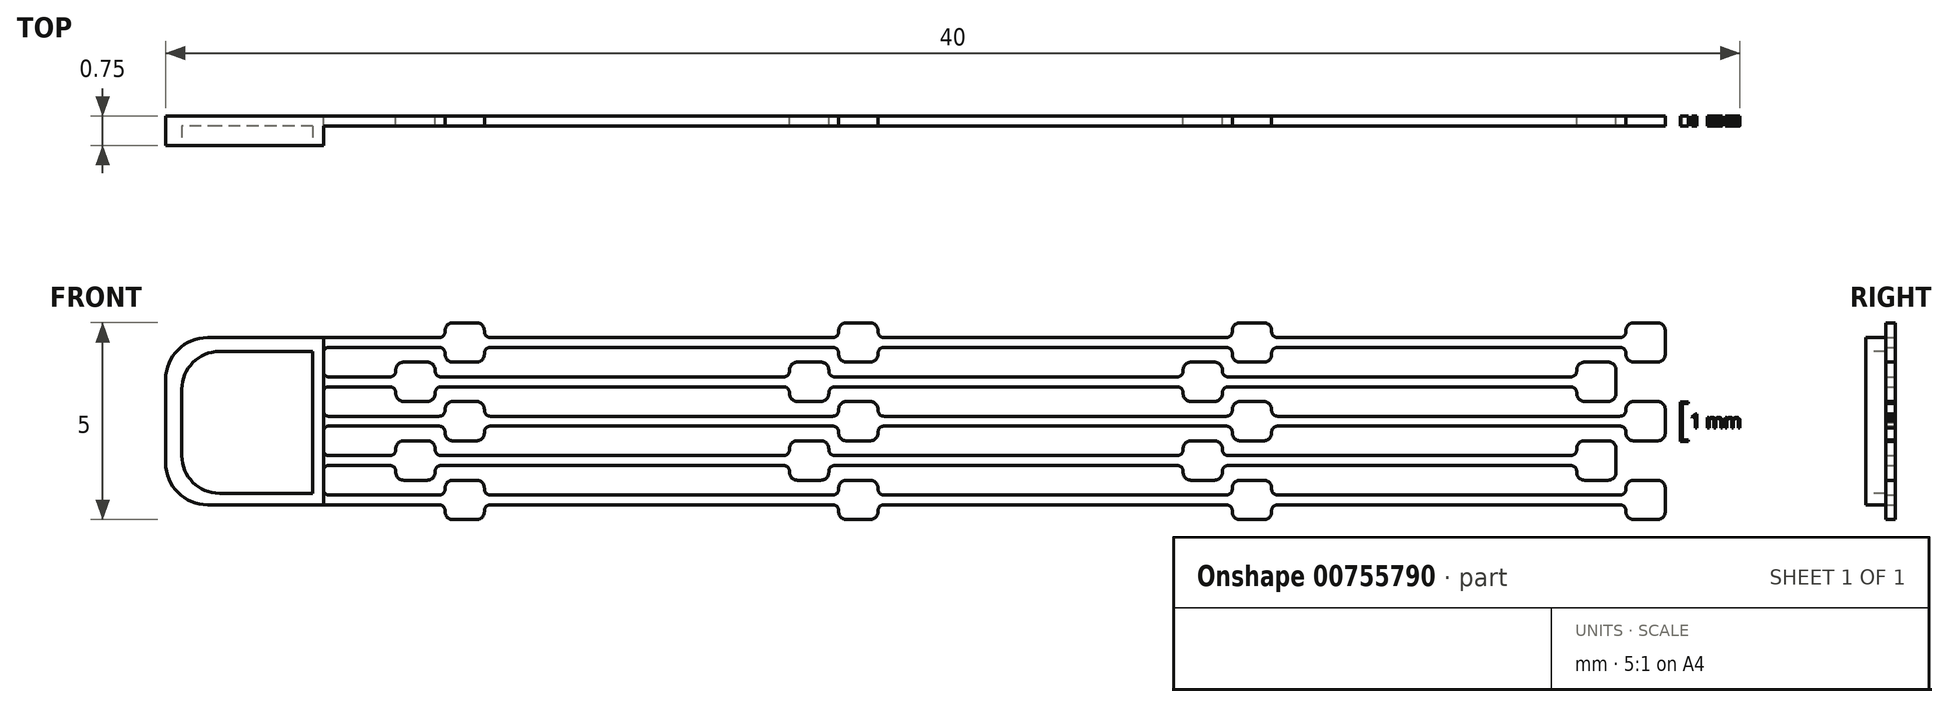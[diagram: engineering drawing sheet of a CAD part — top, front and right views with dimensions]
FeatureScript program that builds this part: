
annotation { "Feature Type Name" : "Feature", "Feature Type Description" : "" }
export const myFeature = defineFeature(function(context is Context, id is Id, definition is map)
    precondition{}
    {
        {
            var Q0;
            Q0=qCreatedBy(makeId("Front.planeOp"),FACE);
            var sketch = newSketch(context, id + "F0", { "sketchPlane" : qUnion([Q0])});
            skLineSegment(sketch, "E0.0.5.4", {"start": v(50.52, 28.02) * mm, "end": v(49.92, 28.02) * mm});
            skLineSegment(sketch, "E0.0.5.5", {"start": v(50.52, 27.02) * mm, "end": v(49.92, 27.02) * mm});
            skLineSegment(sketch, "E0.0.5.6", {"start": v(49.57, 27.4) * mm, "end": v(49.13, 27.4) * mm});
            skLineSegment(sketch, "E0.0.5.7", {"start": v(49.57, 27.64) * mm, "end": v(49.13, 27.64) * mm});
            skPoint(sketch, "E0.0.5.9", {"position": v(49.72, 27.64) * mm});
            skPoint(sketch, "E0.0.5.10", {"position": v(49.72, 28.02) * mm});
            skPoint(sketch, "E0.0.5.11", {"position": v(50.72, 27.4) * mm});
            skPoint(sketch, "E0.0.5.12", {"position": v(50.72, 28.02) * mm});
            skPoint(sketch, "E0.0.5.13", {"position": v(50.72, 27.64) * mm});
            skPoint(sketch, "E0.0.5.15", {"position": v(50.22, 27.52) * mm});
            skLineSegment(sketch, "E0.0.5.18", {"start": v(49.13, 27.4) * mm, "end": v(47.89, 27.4) * mm});
            skLineSegment(sketch, "E0.0.5.19", {"start": v(49.13, 27.64) * mm, "end": v(47.89, 27.64) * mm});
            skPoint(sketch, "E0.0.5.29", {"position": v(49.72, 27.4) * mm});
            skPoint(sketch, "E0.0.5.31", {"position": v(50.22, 27.52) * mm});
            skLineSegment(sketch, "E0.0.5.32", {"start": v(51.17, 27.4) * mm, "end": v(50.87, 27.4) * mm});
            skLineSegment(sketch, "E0.0.5.33", {"start": v(51.17, 27.64) * mm, "end": v(50.87, 27.64) * mm});
            skArc(sketch, "E0.0.5.34", {"start": v(50.72, 27.8) * mm, "mid": v(50.77, 27.69) * mm, "end": v(50.87, 27.64) * mm});
            skArc(sketch, "E0.0.5.41", {"start": v(50.52, 27.02) * mm, "mid": v(50.66, 27.08) * mm, "end": v(50.72, 27.22) * mm});
            skArc(sketch, "E0.0.5.44", {"start": v(49.72, 27.22) * mm, "mid": v(49.78, 27.08) * mm, "end": v(49.92, 27.02) * mm});
            skArc(sketch, "E0.0.5.45", {"start": v(49.92, 28.02) * mm, "mid": v(49.78, 27.96) * mm, "end": v(49.72, 27.82) * mm});
            skArc(sketch, "E0.0.5.46", {"start": v(50.72, 27.82) * mm, "mid": v(50.66, 27.96) * mm, "end": v(50.52, 28.02) * mm});
            skLineSegment(sketch, "E0.0.5.49", {"start": v(49.72, 27.22) * mm, "end": v(49.72, 27.24) * mm});
            skLineSegment(sketch, "E0.0.5.50", {"start": v(50.72, 27.22) * mm, "end": v(50.72, 27.24) * mm});
            skArc(sketch, "E0.0.5.55", {"start": v(49.72, 27.24) * mm, "mid": v(49.68, 27.35) * mm, "end": v(49.57, 27.4) * mm});
            skArc(sketch, "E0.0.5.56", {"start": v(50.87, 27.4) * mm, "mid": v(50.77, 27.35) * mm, "end": v(50.72, 27.24) * mm});
            skLineSegment(sketch, "E0.0.5.57", {"start": v(49.72, 27.8) * mm, "end": v(49.72, 27.82) * mm});
            skLineSegment(sketch, "E0.0.5.60", {"start": v(50.72, 27.8) * mm, "end": v(50.72, 27.82) * mm});
            skArc(sketch, "E0.0.5.61", {"start": v(49.57, 27.64) * mm, "mid": v(49.68, 27.69) * mm, "end": v(49.72, 27.8) * mm});
            skLineSegment(sketch, "E0.0.6.0", {"start": v(47.89, 28.4) * mm, "end": v(48.32, 28.4) * mm});
            skLineSegment(sketch, "E0.0.6.1", {"start": v(47.89, 28.64) * mm, "end": v(48.32, 28.64) * mm});
            skLineSegment(sketch, "E0.0.6.2", {"start": v(49.27, 29.02) * mm, "end": v(48.67, 29.02) * mm});
            skLineSegment(sketch, "E0.0.6.3", {"start": v(49.27, 28.02) * mm, "end": v(48.67, 28.02) * mm});
            skLineSegment(sketch, "E0.0.6.4", {"start": v(50.52, 30.02) * mm, "end": v(49.92, 30.02) * mm});
            skLineSegment(sketch, "E0.0.6.5", {"start": v(50.52, 29.02) * mm, "end": v(49.92, 29.02) * mm});
            skLineSegment(sketch, "E0.0.6.6", {"start": v(49.57, 29.4) * mm, "end": v(49.13, 29.4) * mm});
            skLineSegment(sketch, "E0.0.6.7", {"start": v(49.57, 29.64) * mm, "end": v(49.13, 29.64) * mm});
            skPoint(sketch, "E0.0.6.8", {"position": v(49.72, 29.02) * mm});
            skPoint(sketch, "E0.0.6.9", {"position": v(49.72, 29.64) * mm});
            skPoint(sketch, "E0.0.6.10", {"position": v(49.72, 30.02) * mm});
            skPoint(sketch, "E0.0.6.11", {"position": v(50.72, 29.4) * mm});
            skPoint(sketch, "E0.0.6.12", {"position": v(50.72, 30.02) * mm});
            skPoint(sketch, "E0.0.6.13", {"position": v(50.72, 29.64) * mm});
            skPoint(sketch, "E0.0.6.14", {"position": v(48.97, 28.52) * mm});
            skPoint(sketch, "E0.0.6.15", {"position": v(50.22, 29.52) * mm});
            skPoint(sketch, "E0.0.6.16", {"position": v(49.47, 28.02) * mm});
            skPoint(sketch, "E0.0.6.17", {"position": v(48.47, 28.4) * mm});
            skLineSegment(sketch, "E0.0.6.18", {"start": v(49.13, 29.4) * mm, "end": v(47.89, 29.4) * mm});
            skLineSegment(sketch, "E0.0.6.19", {"start": v(49.13, 29.64) * mm, "end": v(47.89, 29.64) * mm});
            skPoint(sketch, "E0.0.6.20", {"position": v(48.47, 28.02) * mm});
            skPoint(sketch, "E0.0.6.21", {"position": v(48.47, 28.64) * mm});
            skLineSegment(sketch, "E0.0.6.22", {"start": v(49.62, 28.4) * mm, "end": v(51.17, 28.4) * mm});
            skPoint(sketch, "E0.0.6.23", {"position": v(48.47, 29.02) * mm});
            skPoint(sketch, "E0.0.6.24", {"position": v(49.47, 28.4) * mm});
            skLineSegment(sketch, "E0.0.6.25", {"start": v(49.62, 28.64) * mm, "end": v(51.17, 28.64) * mm});
            skPoint(sketch, "E0.0.6.26", {"position": v(49.47, 29.02) * mm});
            skPoint(sketch, "E0.0.6.27", {"position": v(49.47, 28.64) * mm});
            skPoint(sketch, "E0.0.6.28", {"position": v(50.72, 29.02) * mm});
            skPoint(sketch, "E0.0.6.29", {"position": v(49.72, 29.4) * mm});
            skPoint(sketch, "E0.0.6.30", {"position": v(48.97, 28.52) * mm});
            skPoint(sketch, "E0.0.6.31", {"position": v(50.22, 29.52) * mm});
            skLineSegment(sketch, "E0.0.6.32", {"start": v(51.17, 29.4) * mm, "end": v(50.87, 29.4) * mm});
            skLineSegment(sketch, "E0.0.6.33", {"start": v(51.17, 29.64) * mm, "end": v(50.87, 29.64) * mm});
            skArc(sketch, "E0.0.6.34", {"start": v(50.72, 29.8) * mm, "mid": v(50.77, 29.69) * mm, "end": v(50.87, 29.64) * mm});
            skArc(sketch, "E0.0.6.35", {"start": v(49.27, 28.02) * mm, "mid": v(49.41, 28.08) * mm, "end": v(49.47, 28.22) * mm});
            skArc(sketch, "E0.0.6.36", {"start": v(48.47, 28.22) * mm, "mid": v(48.53, 28.08) * mm, "end": v(48.67, 28.02) * mm});
            skArc(sketch, "E0.0.6.37", {"start": v(48.67, 29.02) * mm, "mid": v(48.53, 28.96) * mm, "end": v(48.47, 28.82) * mm});
            skArc(sketch, "E0.0.6.39", {"start": v(49.47, 28.82) * mm, "mid": v(49.41, 28.96) * mm, "end": v(49.27, 29.02) * mm});
            skArc(sketch, "E0.0.6.41", {"start": v(50.52, 29.02) * mm, "mid": v(50.66, 29.08) * mm, "end": v(50.72, 29.22) * mm});
            skArc(sketch, "E0.0.6.44", {"start": v(49.72, 29.22) * mm, "mid": v(49.78, 29.08) * mm, "end": v(49.92, 29.02) * mm});
            skArc(sketch, "E0.0.6.45", {"start": v(49.92, 30.02) * mm, "mid": v(49.78, 29.96) * mm, "end": v(49.72, 29.82) * mm});
            skArc(sketch, "E0.0.6.46", {"start": v(50.72, 29.82) * mm, "mid": v(50.66, 29.96) * mm, "end": v(50.52, 30.02) * mm});
            skArc(sketch, "E0.0.6.47", {"start": v(48.47, 28.24) * mm, "mid": v(48.43, 28.35) * mm, "end": v(48.32, 28.4) * mm});
            skArc(sketch, "E0.0.6.48", {"start": v(49.62, 28.4) * mm, "mid": v(49.52, 28.35) * mm, "end": v(49.47, 28.24) * mm});
            skLineSegment(sketch, "E0.0.6.49", {"start": v(49.72, 29.22) * mm, "end": v(49.72, 29.24) * mm});
            skLineSegment(sketch, "E0.0.6.50", {"start": v(50.72, 29.22) * mm, "end": v(50.72, 29.24) * mm});
            skArc(sketch, "E0.0.6.51", {"start": v(48.32, 28.64) * mm, "mid": v(48.43, 28.69) * mm, "end": v(48.47, 28.8) * mm});
            skLineSegment(sketch, "E0.0.6.52", {"start": v(48.47, 28.8) * mm, "end": v(48.47, 28.82) * mm});
            skArc(sketch, "E0.0.6.53", {"start": v(49.47, 28.8) * mm, "mid": v(49.52, 28.69) * mm, "end": v(49.62, 28.64) * mm});
            skLineSegment(sketch, "E0.0.6.54", {"start": v(49.47, 28.8) * mm, "end": v(49.47, 28.82) * mm});
            skArc(sketch, "E0.0.6.55", {"start": v(49.72, 29.24) * mm, "mid": v(49.68, 29.35) * mm, "end": v(49.57, 29.4) * mm});
            skArc(sketch, "E0.0.6.56", {"start": v(50.87, 29.4) * mm, "mid": v(50.77, 29.35) * mm, "end": v(50.72, 29.24) * mm});
            skLineSegment(sketch, "E0.0.6.57", {"start": v(49.72, 29.8) * mm, "end": v(49.72, 29.82) * mm});
            skLineSegment(sketch, "E0.0.6.58", {"start": v(48.47, 28.22) * mm, "end": v(48.47, 28.24) * mm});
            skLineSegment(sketch, "E0.0.6.59", {"start": v(49.47, 28.22) * mm, "end": v(49.47, 28.24) * mm});
            skLineSegment(sketch, "E0.0.6.60", {"start": v(50.72, 29.8) * mm, "end": v(50.72, 29.82) * mm});
            skArc(sketch, "E0.0.6.61", {"start": v(49.57, 29.64) * mm, "mid": v(49.68, 29.69) * mm, "end": v(49.72, 29.8) * mm});
            skLineSegment(sketch, "E0.0.7.0", {"start": v(47.89, 30.4) * mm, "end": v(48.32, 30.4) * mm});
            skLineSegment(sketch, "E0.0.7.1", {"start": v(47.89, 30.64) * mm, "end": v(48.32, 30.64) * mm});
            skLineSegment(sketch, "E0.0.7.2", {"start": v(49.27, 31.02) * mm, "end": v(48.67, 31.02) * mm});
            skLineSegment(sketch, "E0.0.7.3", {"start": v(49.27, 30.02) * mm, "end": v(48.67, 30.02) * mm});
            skLineSegment(sketch, "E0.0.7.4", {"start": v(50.52, 32.02) * mm, "end": v(49.92, 32.02) * mm});
            skLineSegment(sketch, "E0.0.7.5", {"start": v(50.52, 31.02) * mm, "end": v(49.92, 31.02) * mm});
            skLineSegment(sketch, "E0.0.7.6", {"start": v(49.57, 31.4) * mm, "end": v(49.13, 31.4) * mm});
            skLineSegment(sketch, "E0.0.7.7", {"start": v(49.57, 31.64) * mm, "end": v(49.13, 31.64) * mm});
            skPoint(sketch, "E0.0.7.8", {"position": v(49.72, 31.02) * mm});
            skPoint(sketch, "E0.0.7.9", {"position": v(49.72, 31.64) * mm});
            skPoint(sketch, "E0.0.7.10", {"position": v(49.72, 32.02) * mm});
            skPoint(sketch, "E0.0.7.11", {"position": v(50.72, 31.4) * mm});
            skPoint(sketch, "E0.0.7.12", {"position": v(50.72, 32.02) * mm});
            skPoint(sketch, "E0.0.7.13", {"position": v(50.72, 31.64) * mm});
            skPoint(sketch, "E0.0.7.14", {"position": v(48.97, 30.52) * mm});
            skPoint(sketch, "E0.0.7.15", {"position": v(50.22, 31.52) * mm});
            skPoint(sketch, "E0.0.7.16", {"position": v(49.47, 30.02) * mm});
            skPoint(sketch, "E0.0.7.17", {"position": v(48.47, 30.4) * mm});
            skLineSegment(sketch, "E0.0.7.18", {"start": v(49.13, 31.4) * mm, "end": v(47.89, 31.4) * mm});
            skLineSegment(sketch, "E0.0.7.19", {"start": v(49.13, 31.64) * mm, "end": v(47.89, 31.64) * mm});
            skPoint(sketch, "E0.0.7.20", {"position": v(48.47, 30.02) * mm});
            skPoint(sketch, "E0.0.7.21", {"position": v(48.47, 30.64) * mm});
            skLineSegment(sketch, "E0.0.7.22", {"start": v(49.62, 30.4) * mm, "end": v(51.17, 30.4) * mm});
            skPoint(sketch, "E0.0.7.23", {"position": v(48.47, 31.02) * mm});
            skPoint(sketch, "E0.0.7.24", {"position": v(49.47, 30.4) * mm});
            skLineSegment(sketch, "E0.0.7.25", {"start": v(49.62, 30.64) * mm, "end": v(51.17, 30.64) * mm});
            skPoint(sketch, "E0.0.7.26", {"position": v(49.47, 31.02) * mm});
            skPoint(sketch, "E0.0.7.27", {"position": v(49.47, 30.64) * mm});
            skPoint(sketch, "E0.0.7.28", {"position": v(50.72, 31.02) * mm});
            skPoint(sketch, "E0.0.7.29", {"position": v(49.72, 31.4) * mm});
            skPoint(sketch, "E0.0.7.30", {"position": v(48.97, 30.52) * mm});
            skPoint(sketch, "E0.0.7.31", {"position": v(50.22, 31.52) * mm});
            skLineSegment(sketch, "E0.0.7.32", {"start": v(51.17, 31.4) * mm, "end": v(50.87, 31.4) * mm});
            skLineSegment(sketch, "E0.0.7.33", {"start": v(51.17, 31.64) * mm, "end": v(50.87, 31.64) * mm});
            skArc(sketch, "E0.0.7.34", {"start": v(50.72, 31.8) * mm, "mid": v(50.77, 31.69) * mm, "end": v(50.87, 31.64) * mm});
            skArc(sketch, "E0.0.7.35", {"start": v(49.27, 30.02) * mm, "mid": v(49.41, 30.08) * mm, "end": v(49.47, 30.22) * mm});
            skArc(sketch, "E0.0.7.36", {"start": v(48.47, 30.22) * mm, "mid": v(48.53, 30.08) * mm, "end": v(48.67, 30.02) * mm});
            skArc(sketch, "E0.0.7.37", {"start": v(48.67, 31.02) * mm, "mid": v(48.53, 30.96) * mm, "end": v(48.47, 30.82) * mm});
            skArc(sketch, "E0.0.7.39", {"start": v(49.47, 30.82) * mm, "mid": v(49.41, 30.96) * mm, "end": v(49.27, 31.02) * mm});
            skArc(sketch, "E0.0.7.41", {"start": v(50.52, 31.02) * mm, "mid": v(50.66, 31.08) * mm, "end": v(50.72, 31.22) * mm});
            skArc(sketch, "E0.0.7.44", {"start": v(49.72, 31.22) * mm, "mid": v(49.78, 31.08) * mm, "end": v(49.92, 31.02) * mm});
            skArc(sketch, "E0.0.7.45", {"start": v(49.92, 32.02) * mm, "mid": v(49.78, 31.96) * mm, "end": v(49.72, 31.82) * mm});
            skArc(sketch, "E0.0.7.46", {"start": v(50.72, 31.82) * mm, "mid": v(50.66, 31.96) * mm, "end": v(50.52, 32.02) * mm});
            skArc(sketch, "E0.0.7.47", {"start": v(48.47, 30.24) * mm, "mid": v(48.43, 30.35) * mm, "end": v(48.32, 30.4) * mm});
            skArc(sketch, "E0.0.7.48", {"start": v(49.62, 30.4) * mm, "mid": v(49.52, 30.35) * mm, "end": v(49.47, 30.24) * mm});
            skLineSegment(sketch, "E0.0.7.49", {"start": v(49.72, 31.22) * mm, "end": v(49.72, 31.24) * mm});
            skLineSegment(sketch, "E0.0.7.50", {"start": v(50.72, 31.22) * mm, "end": v(50.72, 31.24) * mm});
            skArc(sketch, "E0.0.7.51", {"start": v(48.32, 30.64) * mm, "mid": v(48.43, 30.69) * mm, "end": v(48.47, 30.8) * mm});
            skLineSegment(sketch, "E0.0.7.52", {"start": v(48.47, 30.8) * mm, "end": v(48.47, 30.82) * mm});
            skArc(sketch, "E0.0.7.53", {"start": v(49.47, 30.8) * mm, "mid": v(49.52, 30.69) * mm, "end": v(49.62, 30.64) * mm});
            skLineSegment(sketch, "E0.0.7.54", {"start": v(49.47, 30.8) * mm, "end": v(49.47, 30.82) * mm});
            skArc(sketch, "E0.0.7.55", {"start": v(49.72, 31.24) * mm, "mid": v(49.68, 31.35) * mm, "end": v(49.57, 31.4) * mm});
            skArc(sketch, "E0.0.7.56", {"start": v(50.87, 31.4) * mm, "mid": v(50.77, 31.35) * mm, "end": v(50.72, 31.24) * mm});
            skLineSegment(sketch, "E0.0.7.57", {"start": v(49.72, 31.8) * mm, "end": v(49.72, 31.82) * mm});
            skLineSegment(sketch, "E0.0.7.58", {"start": v(48.47, 30.22) * mm, "end": v(48.47, 30.24) * mm});
            skLineSegment(sketch, "E0.0.7.59", {"start": v(49.47, 30.22) * mm, "end": v(49.47, 30.24) * mm});
            skLineSegment(sketch, "E0.0.7.60", {"start": v(50.72, 31.8) * mm, "end": v(50.72, 31.82) * mm});
            skArc(sketch, "E0.0.7.61", {"start": v(49.57, 31.64) * mm, "mid": v(49.68, 31.69) * mm, "end": v(49.72, 31.8) * mm});
            skPoint(sketch, "E1.1.0.2", {"position": v(59.72, 32.02) * mm});
            skPoint(sketch, "E1.1.0.3", {"position": v(60.72, 32.02) * mm});
            skPoint(sketch, "E1.1.0.6", {"position": v(60.72, 31.64) * mm});
            skPoint(sketch, "E1.1.0.8", {"position": v(58.47, 28.02) * mm});
            skPoint(sketch, "E1.1.0.11", {"position": v(60.22, 31.52) * mm});
            skPoint(sketch, "E1.1.0.14", {"position": v(59.47, 30.02) * mm});
            skPoint(sketch, "E1.1.0.15", {"position": v(58.47, 29.02) * mm});
            skPoint(sketch, "E1.1.0.17", {"position": v(59.72, 28.02) * mm});
            skPoint(sketch, "E1.1.0.20", {"position": v(58.47, 30.02) * mm});
            skPoint(sketch, "E1.1.0.21", {"position": v(60.72, 27.4) * mm});
            skPoint(sketch, "E1.1.0.22", {"position": v(58.47, 30.64) * mm});
            skPoint(sketch, "E1.1.0.32", {"position": v(60.72, 29.02) * mm});
            skPoint(sketch, "E1.1.0.33", {"position": v(58.47, 31.02) * mm});
            skPoint(sketch, "E1.1.0.34", {"position": v(60.72, 28.02) * mm});
            skPoint(sketch, "E1.1.0.35", {"position": v(59.72, 29.02) * mm});
            skPoint(sketch, "E1.1.0.38", {"position": v(59.72, 31.64) * mm});
            skPoint(sketch, "E1.1.0.39", {"position": v(60.72, 29.64) * mm});
            skPoint(sketch, "E1.1.0.43", {"position": v(60.22, 31.52) * mm});
            skPoint(sketch, "E1.1.0.44", {"position": v(60.72, 31.4) * mm});
            skPoint(sketch, "E1.1.0.49", {"position": v(58.47, 28.4) * mm});
            skPoint(sketch, "E1.1.0.52", {"position": v(58.97, 30.52) * mm});
            skPoint(sketch, "E1.1.0.57", {"position": v(58.47, 28.64) * mm});
            skPoint(sketch, "E1.1.0.67", {"position": v(59.72, 27.64) * mm});
            skPoint(sketch, "E1.1.0.68", {"position": v(58.47, 30.4) * mm});
            skPoint(sketch, "E1.1.0.69", {"position": v(59.47, 28.4) * mm});
            skPoint(sketch, "E1.1.0.71", {"position": v(60.22, 27.52) * mm});
            skPoint(sketch, "E1.1.0.72", {"position": v(59.47, 28.64) * mm});
            skPoint(sketch, "E1.1.0.78", {"position": v(59.72, 31.4) * mm});
            skPoint(sketch, "E1.1.0.80", {"position": v(60.72, 30.02) * mm});
            skPoint(sketch, "E1.1.0.82", {"position": v(60.22, 27.52) * mm});
            skPoint(sketch, "E1.1.0.83", {"position": v(60.72, 29.4) * mm});
            skPoint(sketch, "E1.1.0.85", {"position": v(60.72, 31.02) * mm});
            skPoint(sketch, "E1.1.0.88", {"position": v(58.97, 28.52) * mm});
            skPoint(sketch, "E1.1.0.90", {"position": v(58.97, 30.52) * mm});
            skPoint(sketch, "E1.1.0.92", {"position": v(60.22, 29.52) * mm});
            skPoint(sketch, "E1.1.0.94", {"position": v(60.72, 27.64) * mm});
            skPoint(sketch, "E1.1.0.106", {"position": v(59.72, 27.4) * mm});
            skPoint(sketch, "E1.1.0.110", {"position": v(59.47, 29.02) * mm});
            skPoint(sketch, "E1.1.0.113", {"position": v(60.22, 29.52) * mm});
            skPoint(sketch, "E1.1.0.117", {"position": v(59.72, 31.02) * mm});
            skPoint(sketch, "E1.1.0.126", {"position": v(59.47, 28.02) * mm});
            skPoint(sketch, "E1.1.0.134", {"position": v(58.97, 28.52) * mm});
            skPoint(sketch, "E1.1.0.141", {"position": v(59.47, 30.64) * mm});
            skPoint(sketch, "E1.1.0.147", {"position": v(59.72, 30.02) * mm});
            skPoint(sketch, "E1.1.0.148", {"position": v(59.47, 31.02) * mm});
            skPoint(sketch, "E1.1.0.154", {"position": v(59.47, 30.4) * mm});
            skPoint(sketch, "E1.1.0.155", {"position": v(59.72, 29.4) * mm});
            skPoint(sketch, "E1.1.0.156", {"position": v(59.72, 29.64) * mm});
            skLineSegment(sketch, "E1.1.0.161", {"start": v(59.13, 31.64) * mm, "end": v(57.89, 31.64) * mm});
            skLineSegment(sketch, "E1.1.0.162", {"start": v(59.13, 31.4) * mm, "end": v(57.89, 31.4) * mm});
            skLineSegment(sketch, "E1.1.0.163", {"start": v(57.89, 30.64) * mm, "end": v(58.32, 30.64) * mm});
            skLineSegment(sketch, "E1.1.0.166", {"start": v(57.89, 30.4) * mm, "end": v(58.32, 30.4) * mm});
            skLineSegment(sketch, "E1.1.0.171", {"start": v(59.13, 29.64) * mm, "end": v(57.89, 29.64) * mm});
            skLineSegment(sketch, "E1.1.0.173", {"start": v(59.13, 29.4) * mm, "end": v(57.89, 29.4) * mm});
            skLineSegment(sketch, "E1.1.0.174", {"start": v(59.13, 27.64) * mm, "end": v(57.89, 27.64) * mm});
            skArc(sketch, "E1.1.0.175", {"start": v(58.47, 28.22) * mm, "mid": v(58.53, 28.08) * mm, "end": v(58.67, 28.02) * mm});
            skLineSegment(sketch, "E1.1.0.176", {"start": v(57.89, 28.4) * mm, "end": v(58.32, 28.4) * mm});
            skLineSegment(sketch, "E1.1.0.177", {"start": v(57.89, 28.64) * mm, "end": v(58.32, 28.64) * mm});
            skLineSegment(sketch, "E1.1.0.180", {"start": v(60.52, 32.02) * mm, "end": v(59.92, 32.02) * mm});
            skLineSegment(sketch, "E1.1.0.185", {"start": v(61.17, 31.64) * mm, "end": v(60.87, 31.64) * mm});
            skLineSegment(sketch, "E1.1.0.194", {"start": v(59.13, 27.4) * mm, "end": v(57.89, 27.4) * mm});
            skLineSegment(sketch, "E1.1.0.205", {"start": v(61.17, 31.4) * mm, "end": v(60.87, 31.4) * mm});
            skArc(sketch, "E1.1.0.215", {"start": v(59.57, 31.64) * mm, "mid": v(59.68, 31.69) * mm, "end": v(59.72, 31.8) * mm});
            skArc(sketch, "E1.1.0.216", {"start": v(60.72, 31.82) * mm, "mid": v(60.66, 31.96) * mm, "end": v(60.52, 32.02) * mm});
            skArc(sketch, "E1.1.0.218", {"start": v(60.72, 31.8) * mm, "mid": v(60.77, 31.69) * mm, "end": v(60.87, 31.64) * mm});
            skLineSegment(sketch, "E1.1.0.222", {"start": v(61.17, 29.64) * mm, "end": v(60.87, 29.64) * mm});
            skLineSegment(sketch, "E1.1.0.228", {"start": v(59.72, 31.8) * mm, "end": v(59.72, 31.82) * mm});
            skLineSegment(sketch, "E1.1.0.229", {"start": v(60.72, 31.8) * mm, "end": v(60.72, 31.82) * mm});
            skLineSegment(sketch, "E1.1.0.230", {"start": v(59.62, 30.64) * mm, "end": v(61.17, 30.64) * mm});
            skArc(sketch, "E1.1.0.231", {"start": v(59.92, 32.02) * mm, "mid": v(59.78, 31.96) * mm, "end": v(59.72, 31.82) * mm});
            skLineSegment(sketch, "E1.1.0.239", {"start": v(59.27, 31.02) * mm, "end": v(58.67, 31.02) * mm});
            skLineSegment(sketch, "E1.1.0.240", {"start": v(61.17, 29.4) * mm, "end": v(60.87, 29.4) * mm});
            skLineSegment(sketch, "E1.1.0.242", {"start": v(59.57, 31.64) * mm, "end": v(59.13, 31.64) * mm});
            skArc(sketch, "E1.1.0.243", {"start": v(59.47, 30.82) * mm, "mid": v(59.41, 30.96) * mm, "end": v(59.27, 31.02) * mm});
            skArc(sketch, "E1.1.0.244", {"start": v(59.72, 31.24) * mm, "mid": v(59.68, 31.35) * mm, "end": v(59.57, 31.4) * mm});
            skArc(sketch, "E1.1.0.246", {"start": v(60.87, 31.4) * mm, "mid": v(60.77, 31.35) * mm, "end": v(60.72, 31.24) * mm});
            skLineSegment(sketch, "E1.1.0.249", {"start": v(59.57, 31.4) * mm, "end": v(59.13, 31.4) * mm});
            skLineSegment(sketch, "E1.1.0.250", {"start": v(60.52, 31.02) * mm, "end": v(59.92, 31.02) * mm});
            skArc(sketch, "E1.1.0.251", {"start": v(60.52, 31.02) * mm, "mid": v(60.66, 31.08) * mm, "end": v(60.72, 31.22) * mm});
            skLineSegment(sketch, "E1.1.0.253", {"start": v(59.62, 30.4) * mm, "end": v(61.17, 30.4) * mm});
            skLineSegment(sketch, "E1.1.0.257", {"start": v(59.72, 31.22) * mm, "end": v(59.72, 31.24) * mm});
            skLineSegment(sketch, "E1.1.0.259", {"start": v(60.72, 31.22) * mm, "end": v(60.72, 31.24) * mm});
            skArc(sketch, "E1.1.0.260", {"start": v(58.32, 30.64) * mm, "mid": v(58.43, 30.69) * mm, "end": v(58.47, 30.8) * mm});
            skArc(sketch, "E1.1.0.264", {"start": v(58.67, 31.02) * mm, "mid": v(58.53, 30.96) * mm, "end": v(58.47, 30.82) * mm});
            skLineSegment(sketch, "E1.1.0.265", {"start": v(59.62, 28.64) * mm, "end": v(61.17, 28.64) * mm});
            skArc(sketch, "E1.1.0.266", {"start": v(59.47, 30.8) * mm, "mid": v(59.52, 30.69) * mm, "end": v(59.62, 30.64) * mm});
            skLineSegment(sketch, "E1.1.0.269", {"start": v(59.47, 30.8) * mm, "end": v(59.47, 30.82) * mm});
            skLineSegment(sketch, "E1.1.0.274", {"start": v(61.17, 27.4) * mm, "end": v(60.87, 27.4) * mm});
            skArc(sketch, "E1.1.0.275", {"start": v(58.47, 30.24) * mm, "mid": v(58.43, 30.35) * mm, "end": v(58.32, 30.4) * mm});
            skLineSegment(sketch, "E1.1.0.276", {"start": v(61.17, 27.64) * mm, "end": v(60.87, 27.64) * mm});
            skArc(sketch, "E1.1.0.278", {"start": v(59.72, 31.22) * mm, "mid": v(59.78, 31.08) * mm, "end": v(59.92, 31.02) * mm});
            skArc(sketch, "E1.1.0.280", {"start": v(59.62, 30.4) * mm, "mid": v(59.52, 30.35) * mm, "end": v(59.47, 30.24) * mm});
            skLineSegment(sketch, "E1.1.0.284", {"start": v(59.62, 28.4) * mm, "end": v(61.17, 28.4) * mm});
            skLineSegment(sketch, "E1.1.0.285", {"start": v(58.47, 30.8) * mm, "end": v(58.47, 30.82) * mm});
            skLineSegment(sketch, "E1.1.0.288", {"start": v(60.52, 29.02) * mm, "end": v(59.92, 29.02) * mm});
            skArc(sketch, "E1.1.0.289", {"start": v(59.47, 28.82) * mm, "mid": v(59.41, 28.96) * mm, "end": v(59.27, 29.02) * mm});
            skLineSegment(sketch, "E1.1.0.290", {"start": v(60.52, 30.02) * mm, "end": v(59.92, 30.02) * mm});
            skLineSegment(sketch, "E1.1.0.292", {"start": v(59.27, 29.02) * mm, "end": v(58.67, 29.02) * mm});
            skLineSegment(sketch, "E1.1.0.293", {"start": v(59.27, 28.02) * mm, "end": v(58.67, 28.02) * mm});
            skLineSegment(sketch, "E1.1.0.295", {"start": v(59.57, 29.64) * mm, "end": v(59.13, 29.64) * mm});
            skArc(sketch, "E1.1.0.298", {"start": v(59.92, 30.02) * mm, "mid": v(59.78, 29.96) * mm, "end": v(59.72, 29.82) * mm});
            skArc(sketch, "E1.1.0.299", {"start": v(59.57, 29.64) * mm, "mid": v(59.68, 29.69) * mm, "end": v(59.72, 29.8) * mm});
            skArc(sketch, "E1.1.0.301", {"start": v(60.72, 29.82) * mm, "mid": v(60.66, 29.96) * mm, "end": v(60.52, 30.02) * mm});
            skArc(sketch, "E1.1.0.304", {"start": v(58.47, 28.24) * mm, "mid": v(58.43, 28.35) * mm, "end": v(58.32, 28.4) * mm});
            skArc(sketch, "E1.1.0.305", {"start": v(58.67, 29.02) * mm, "mid": v(58.53, 28.96) * mm, "end": v(58.47, 28.82) * mm});
            skArc(sketch, "E1.1.0.308", {"start": v(59.62, 28.4) * mm, "mid": v(59.52, 28.35) * mm, "end": v(59.47, 28.24) * mm});
            skLineSegment(sketch, "E1.1.0.311", {"start": v(59.27, 30.02) * mm, "end": v(58.67, 30.02) * mm});
            skLineSegment(sketch, "E1.1.0.312", {"start": v(59.72, 29.22) * mm, "end": v(59.72, 29.24) * mm});
            skLineSegment(sketch, "E1.1.0.315", {"start": v(60.72, 29.22) * mm, "end": v(60.72, 29.24) * mm});
            skArc(sketch, "E1.1.0.316", {"start": v(60.72, 29.8) * mm, "mid": v(60.77, 29.69) * mm, "end": v(60.87, 29.64) * mm});
            skArc(sketch, "E1.1.0.317", {"start": v(59.92, 28.02) * mm, "mid": v(59.78, 27.96) * mm, "end": v(59.72, 27.82) * mm});
            skLineSegment(sketch, "E1.1.0.326", {"start": v(58.47, 30.22) * mm, "end": v(58.47, 30.24) * mm});
            skLineSegment(sketch, "E1.1.0.327", {"start": v(58.47, 28.8) * mm, "end": v(58.47, 28.82) * mm});
            skArc(sketch, "E1.1.0.328", {"start": v(60.72, 27.82) * mm, "mid": v(60.66, 27.96) * mm, "end": v(60.52, 28.02) * mm});
            skArc(sketch, "E1.1.0.333", {"start": v(59.27, 28.02) * mm, "mid": v(59.41, 28.08) * mm, "end": v(59.47, 28.22) * mm});
            skArc(sketch, "E1.1.0.337", {"start": v(60.52, 29.02) * mm, "mid": v(60.66, 29.08) * mm, "end": v(60.72, 29.22) * mm});
            skLineSegment(sketch, "E1.1.0.340", {"start": v(59.72, 29.8) * mm, "end": v(59.72, 29.82) * mm});
            skLineSegment(sketch, "E1.1.0.343", {"start": v(59.57, 29.4) * mm, "end": v(59.13, 29.4) * mm});
            skLineSegment(sketch, "E1.1.0.345", {"start": v(58.47, 28.22) * mm, "end": v(58.47, 28.24) * mm});
            skLineSegment(sketch, "E1.1.0.349", {"start": v(59.47, 28.22) * mm, "end": v(59.47, 28.24) * mm});
            skArc(sketch, "E1.1.0.356", {"start": v(59.72, 29.22) * mm, "mid": v(59.78, 29.08) * mm, "end": v(59.92, 29.02) * mm});
            skLineSegment(sketch, "E1.1.0.357", {"start": v(60.72, 29.8) * mm, "end": v(60.72, 29.82) * mm});
            skArc(sketch, "E1.1.0.363", {"start": v(59.27, 30.02) * mm, "mid": v(59.41, 30.08) * mm, "end": v(59.47, 30.22) * mm});
            skLineSegment(sketch, "E1.1.0.369", {"start": v(60.52, 28.02) * mm, "end": v(59.92, 28.02) * mm});
            skArc(sketch, "E1.1.0.371", {"start": v(58.47, 30.22) * mm, "mid": v(58.53, 30.08) * mm, "end": v(58.67, 30.02) * mm});
            skArc(sketch, "E1.1.0.374", {"start": v(60.52, 27.02) * mm, "mid": v(60.66, 27.08) * mm, "end": v(60.72, 27.22) * mm});
            skLineSegment(sketch, "E1.1.0.375", {"start": v(60.52, 27.02) * mm, "end": v(59.92, 27.02) * mm});
            skLineSegment(sketch, "E1.1.0.377", {"start": v(59.57, 27.4) * mm, "end": v(59.13, 27.4) * mm});
            skLineSegment(sketch, "E1.1.0.382", {"start": v(59.57, 27.64) * mm, "end": v(59.13, 27.64) * mm});
            skArc(sketch, "E1.1.0.383", {"start": v(59.47, 28.8) * mm, "mid": v(59.52, 28.69) * mm, "end": v(59.62, 28.64) * mm});
            skLineSegment(sketch, "E1.1.0.385", {"start": v(60.72, 27.8) * mm, "end": v(60.72, 27.82) * mm});
            skArc(sketch, "E1.1.0.386", {"start": v(59.72, 27.22) * mm, "mid": v(59.78, 27.08) * mm, "end": v(59.92, 27.02) * mm});
            skArc(sketch, "E1.1.0.390", {"start": v(59.57, 27.64) * mm, "mid": v(59.68, 27.69) * mm, "end": v(59.72, 27.8) * mm});
            skArc(sketch, "E1.1.0.397", {"start": v(58.32, 28.64) * mm, "mid": v(58.43, 28.69) * mm, "end": v(58.47, 28.8) * mm});
            skArc(sketch, "E1.1.0.399", {"start": v(60.72, 27.8) * mm, "mid": v(60.77, 27.69) * mm, "end": v(60.87, 27.64) * mm});
            skLineSegment(sketch, "E1.1.0.402", {"start": v(59.47, 28.8) * mm, "end": v(59.47, 28.82) * mm});
            skArc(sketch, "E1.1.0.403", {"start": v(60.87, 29.4) * mm, "mid": v(60.77, 29.35) * mm, "end": v(60.72, 29.24) * mm});
            skArc(sketch, "E1.1.0.410", {"start": v(59.72, 29.24) * mm, "mid": v(59.68, 29.35) * mm, "end": v(59.57, 29.4) * mm});
            skArc(sketch, "E1.1.0.418", {"start": v(59.72, 27.24) * mm, "mid": v(59.68, 27.35) * mm, "end": v(59.57, 27.4) * mm});
            skArc(sketch, "E1.1.0.421", {"start": v(60.87, 27.4) * mm, "mid": v(60.77, 27.35) * mm, "end": v(60.72, 27.24) * mm});
            skLineSegment(sketch, "E1.1.0.423", {"start": v(59.72, 27.8) * mm, "end": v(59.72, 27.82) * mm});
            skLineSegment(sketch, "E1.1.0.426", {"start": v(59.47, 30.22) * mm, "end": v(59.47, 30.24) * mm});
            skLineSegment(sketch, "E1.1.0.430", {"start": v(59.72, 27.22) * mm, "end": v(59.72, 27.24) * mm});
            skLineSegment(sketch, "E1.1.0.432", {"start": v(60.72, 27.22) * mm, "end": v(60.72, 27.24) * mm});
            skPoint(sketch, "E1.2.0.2", {"position": v(69.72, 32.02) * mm});
            skPoint(sketch, "E1.2.0.3", {"position": v(70.72, 32.02) * mm});
            skPoint(sketch, "E1.2.0.6", {"position": v(70.72, 31.64) * mm});
            skPoint(sketch, "E1.2.0.8", {"position": v(68.47, 28.02) * mm});
            skPoint(sketch, "E1.2.0.11", {"position": v(70.22, 31.52) * mm});
            skPoint(sketch, "E1.2.0.14", {"position": v(69.47, 30.02) * mm});
            skPoint(sketch, "E1.2.0.15", {"position": v(68.47, 29.02) * mm});
            skPoint(sketch, "E1.2.0.17", {"position": v(69.72, 28.02) * mm});
            skPoint(sketch, "E1.2.0.20", {"position": v(68.47, 30.02) * mm});
            skPoint(sketch, "E1.2.0.21", {"position": v(70.72, 27.4) * mm});
            skPoint(sketch, "E1.2.0.22", {"position": v(68.47, 30.64) * mm});
            skPoint(sketch, "E1.2.0.32", {"position": v(70.72, 29.02) * mm});
            skPoint(sketch, "E1.2.0.33", {"position": v(68.47, 31.02) * mm});
            skPoint(sketch, "E1.2.0.34", {"position": v(70.72, 28.02) * mm});
            skPoint(sketch, "E1.2.0.35", {"position": v(69.72, 29.02) * mm});
            skPoint(sketch, "E1.2.0.38", {"position": v(69.72, 31.64) * mm});
            skPoint(sketch, "E1.2.0.39", {"position": v(70.72, 29.64) * mm});
            skPoint(sketch, "E1.2.0.43", {"position": v(70.22, 31.52) * mm});
            skPoint(sketch, "E1.2.0.44", {"position": v(70.72, 31.4) * mm});
            skPoint(sketch, "E1.2.0.49", {"position": v(68.47, 28.4) * mm});
            skPoint(sketch, "E1.2.0.52", {"position": v(68.97, 30.52) * mm});
            skPoint(sketch, "E1.2.0.57", {"position": v(68.47, 28.64) * mm});
            skPoint(sketch, "E1.2.0.67", {"position": v(69.72, 27.64) * mm});
            skPoint(sketch, "E1.2.0.68", {"position": v(68.47, 30.4) * mm});
            skPoint(sketch, "E1.2.0.69", {"position": v(69.47, 28.4) * mm});
            skPoint(sketch, "E1.2.0.71", {"position": v(70.22, 27.52) * mm});
            skPoint(sketch, "E1.2.0.72", {"position": v(69.47, 28.64) * mm});
            skPoint(sketch, "E1.2.0.78", {"position": v(69.72, 31.4) * mm});
            skPoint(sketch, "E1.2.0.80", {"position": v(70.72, 30.02) * mm});
            skPoint(sketch, "E1.2.0.82", {"position": v(70.22, 27.52) * mm});
            skPoint(sketch, "E1.2.0.83", {"position": v(70.72, 29.4) * mm});
            skPoint(sketch, "E1.2.0.85", {"position": v(70.72, 31.02) * mm});
            skPoint(sketch, "E1.2.0.88", {"position": v(68.97, 28.52) * mm});
            skPoint(sketch, "E1.2.0.90", {"position": v(68.97, 30.52) * mm});
            skPoint(sketch, "E1.2.0.92", {"position": v(70.22, 29.52) * mm});
            skPoint(sketch, "E1.2.0.94", {"position": v(70.72, 27.64) * mm});
            skPoint(sketch, "E1.2.0.106", {"position": v(69.72, 27.4) * mm});
            skPoint(sketch, "E1.2.0.110", {"position": v(69.47, 29.02) * mm});
            skPoint(sketch, "E1.2.0.113", {"position": v(70.22, 29.52) * mm});
            skPoint(sketch, "E1.2.0.117", {"position": v(69.72, 31.02) * mm});
            skPoint(sketch, "E1.2.0.126", {"position": v(69.47, 28.02) * mm});
            skPoint(sketch, "E1.2.0.134", {"position": v(68.97, 28.52) * mm});
            skPoint(sketch, "E1.2.0.141", {"position": v(69.47, 30.64) * mm});
            skPoint(sketch, "E1.2.0.147", {"position": v(69.72, 30.02) * mm});
            skPoint(sketch, "E1.2.0.148", {"position": v(69.47, 31.02) * mm});
            skPoint(sketch, "E1.2.0.154", {"position": v(69.47, 30.4) * mm});
            skPoint(sketch, "E1.2.0.155", {"position": v(69.72, 29.4) * mm});
            skPoint(sketch, "E1.2.0.156", {"position": v(69.72, 29.64) * mm});
            skLineSegment(sketch, "E1.2.0.161", {"start": v(69.13, 31.64) * mm, "end": v(67.89, 31.64) * mm});
            skLineSegment(sketch, "E1.2.0.162", {"start": v(69.13, 31.4) * mm, "end": v(67.89, 31.4) * mm});
            skLineSegment(sketch, "E1.2.0.163", {"start": v(67.89, 30.64) * mm, "end": v(68.32, 30.64) * mm});
            skLineSegment(sketch, "E1.2.0.166", {"start": v(67.89, 30.4) * mm, "end": v(68.32, 30.4) * mm});
            skLineSegment(sketch, "E1.2.0.171", {"start": v(69.13, 29.64) * mm, "end": v(67.89, 29.64) * mm});
            skLineSegment(sketch, "E1.2.0.173", {"start": v(69.13, 29.4) * mm, "end": v(67.89, 29.4) * mm});
            skLineSegment(sketch, "E1.2.0.174", {"start": v(69.13, 27.64) * mm, "end": v(67.89, 27.64) * mm});
            skArc(sketch, "E1.2.0.175", {"start": v(68.47, 28.22) * mm, "mid": v(68.53, 28.08) * mm, "end": v(68.67, 28.02) * mm});
            skLineSegment(sketch, "E1.2.0.176", {"start": v(67.89, 28.4) * mm, "end": v(68.32, 28.4) * mm});
            skLineSegment(sketch, "E1.2.0.177", {"start": v(67.89, 28.64) * mm, "end": v(68.32, 28.64) * mm});
            skLineSegment(sketch, "E1.2.0.180", {"start": v(70.52, 32.02) * mm, "end": v(69.92, 32.02) * mm});
            skLineSegment(sketch, "E1.2.0.185", {"start": v(71.17, 31.64) * mm, "end": v(70.87, 31.64) * mm});
            skLineSegment(sketch, "E1.2.0.194", {"start": v(69.13, 27.4) * mm, "end": v(67.89, 27.4) * mm});
            skLineSegment(sketch, "E1.2.0.205", {"start": v(71.17, 31.4) * mm, "end": v(70.87, 31.4) * mm});
            skArc(sketch, "E1.2.0.215", {"start": v(69.57, 31.64) * mm, "mid": v(69.68, 31.69) * mm, "end": v(69.72, 31.8) * mm});
            skArc(sketch, "E1.2.0.216", {"start": v(70.72, 31.82) * mm, "mid": v(70.66, 31.96) * mm, "end": v(70.52, 32.02) * mm});
            skArc(sketch, "E1.2.0.218", {"start": v(70.72, 31.8) * mm, "mid": v(70.77, 31.69) * mm, "end": v(70.87, 31.64) * mm});
            skLineSegment(sketch, "E1.2.0.222", {"start": v(71.17, 29.64) * mm, "end": v(70.87, 29.64) * mm});
            skLineSegment(sketch, "E1.2.0.228", {"start": v(69.72, 31.8) * mm, "end": v(69.72, 31.82) * mm});
            skLineSegment(sketch, "E1.2.0.229", {"start": v(70.72, 31.8) * mm, "end": v(70.72, 31.82) * mm});
            skLineSegment(sketch, "E1.2.0.230", {"start": v(69.62, 30.64) * mm, "end": v(71.17, 30.64) * mm});
            skArc(sketch, "E1.2.0.231", {"start": v(69.92, 32.02) * mm, "mid": v(69.78, 31.96) * mm, "end": v(69.72, 31.82) * mm});
            skLineSegment(sketch, "E1.2.0.239", {"start": v(69.27, 31.02) * mm, "end": v(68.67, 31.02) * mm});
            skLineSegment(sketch, "E1.2.0.240", {"start": v(71.17, 29.4) * mm, "end": v(70.87, 29.4) * mm});
            skLineSegment(sketch, "E1.2.0.242", {"start": v(69.57, 31.64) * mm, "end": v(69.13, 31.64) * mm});
            skArc(sketch, "E1.2.0.243", {"start": v(69.47, 30.82) * mm, "mid": v(69.41, 30.96) * mm, "end": v(69.27, 31.02) * mm});
            skArc(sketch, "E1.2.0.244", {"start": v(69.72, 31.24) * mm, "mid": v(69.68, 31.35) * mm, "end": v(69.57, 31.4) * mm});
            skArc(sketch, "E1.2.0.246", {"start": v(70.87, 31.4) * mm, "mid": v(70.77, 31.35) * mm, "end": v(70.72, 31.24) * mm});
            skLineSegment(sketch, "E1.2.0.249", {"start": v(69.57, 31.4) * mm, "end": v(69.13, 31.4) * mm});
            skLineSegment(sketch, "E1.2.0.250", {"start": v(70.52, 31.02) * mm, "end": v(69.92, 31.02) * mm});
            skArc(sketch, "E1.2.0.251", {"start": v(70.52, 31.02) * mm, "mid": v(70.66, 31.08) * mm, "end": v(70.72, 31.22) * mm});
            skLineSegment(sketch, "E1.2.0.253", {"start": v(69.62, 30.4) * mm, "end": v(71.17, 30.4) * mm});
            skLineSegment(sketch, "E1.2.0.257", {"start": v(69.72, 31.22) * mm, "end": v(69.72, 31.24) * mm});
            skLineSegment(sketch, "E1.2.0.259", {"start": v(70.72, 31.22) * mm, "end": v(70.72, 31.24) * mm});
            skArc(sketch, "E1.2.0.260", {"start": v(68.32, 30.64) * mm, "mid": v(68.43, 30.69) * mm, "end": v(68.47, 30.8) * mm});
            skArc(sketch, "E1.2.0.264", {"start": v(68.67, 31.02) * mm, "mid": v(68.53, 30.96) * mm, "end": v(68.47, 30.82) * mm});
            skLineSegment(sketch, "E1.2.0.265", {"start": v(69.62, 28.64) * mm, "end": v(71.17, 28.64) * mm});
            skArc(sketch, "E1.2.0.266", {"start": v(69.47, 30.8) * mm, "mid": v(69.52, 30.69) * mm, "end": v(69.62, 30.64) * mm});
            skLineSegment(sketch, "E1.2.0.269", {"start": v(69.47, 30.8) * mm, "end": v(69.47, 30.82) * mm});
            skLineSegment(sketch, "E1.2.0.274", {"start": v(71.17, 27.4) * mm, "end": v(70.87, 27.4) * mm});
            skArc(sketch, "E1.2.0.275", {"start": v(68.47, 30.24) * mm, "mid": v(68.43, 30.35) * mm, "end": v(68.32, 30.4) * mm});
            skLineSegment(sketch, "E1.2.0.276", {"start": v(71.17, 27.64) * mm, "end": v(70.87, 27.64) * mm});
            skArc(sketch, "E1.2.0.278", {"start": v(69.72, 31.22) * mm, "mid": v(69.78, 31.08) * mm, "end": v(69.92, 31.02) * mm});
            skArc(sketch, "E1.2.0.280", {"start": v(69.62, 30.4) * mm, "mid": v(69.52, 30.35) * mm, "end": v(69.47, 30.24) * mm});
            skLineSegment(sketch, "E1.2.0.284", {"start": v(69.62, 28.4) * mm, "end": v(71.17, 28.4) * mm});
            skLineSegment(sketch, "E1.2.0.285", {"start": v(68.47, 30.8) * mm, "end": v(68.47, 30.82) * mm});
            skLineSegment(sketch, "E1.2.0.288", {"start": v(70.52, 29.02) * mm, "end": v(69.92, 29.02) * mm});
            skArc(sketch, "E1.2.0.289", {"start": v(69.47, 28.82) * mm, "mid": v(69.41, 28.96) * mm, "end": v(69.27, 29.02) * mm});
            skLineSegment(sketch, "E1.2.0.290", {"start": v(70.52, 30.02) * mm, "end": v(69.92, 30.02) * mm});
            skLineSegment(sketch, "E1.2.0.292", {"start": v(69.27, 29.02) * mm, "end": v(68.67, 29.02) * mm});
            skLineSegment(sketch, "E1.2.0.293", {"start": v(69.27, 28.02) * mm, "end": v(68.67, 28.02) * mm});
            skLineSegment(sketch, "E1.2.0.295", {"start": v(69.57, 29.64) * mm, "end": v(69.13, 29.64) * mm});
            skArc(sketch, "E1.2.0.298", {"start": v(69.92, 30.02) * mm, "mid": v(69.78, 29.96) * mm, "end": v(69.72, 29.82) * mm});
            skArc(sketch, "E1.2.0.299", {"start": v(69.57, 29.64) * mm, "mid": v(69.68, 29.69) * mm, "end": v(69.72, 29.8) * mm});
            skArc(sketch, "E1.2.0.301", {"start": v(70.72, 29.82) * mm, "mid": v(70.66, 29.96) * mm, "end": v(70.52, 30.02) * mm});
            skArc(sketch, "E1.2.0.304", {"start": v(68.47, 28.24) * mm, "mid": v(68.43, 28.35) * mm, "end": v(68.32, 28.4) * mm});
            skArc(sketch, "E1.2.0.305", {"start": v(68.67, 29.02) * mm, "mid": v(68.53, 28.96) * mm, "end": v(68.47, 28.82) * mm});
            skArc(sketch, "E1.2.0.308", {"start": v(69.62, 28.4) * mm, "mid": v(69.52, 28.35) * mm, "end": v(69.47, 28.24) * mm});
            skLineSegment(sketch, "E1.2.0.311", {"start": v(69.27, 30.02) * mm, "end": v(68.67, 30.02) * mm});
            skLineSegment(sketch, "E1.2.0.312", {"start": v(69.72, 29.22) * mm, "end": v(69.72, 29.24) * mm});
            skLineSegment(sketch, "E1.2.0.315", {"start": v(70.72, 29.22) * mm, "end": v(70.72, 29.24) * mm});
            skArc(sketch, "E1.2.0.316", {"start": v(70.72, 29.8) * mm, "mid": v(70.77, 29.69) * mm, "end": v(70.87, 29.64) * mm});
            skArc(sketch, "E1.2.0.317", {"start": v(69.92, 28.02) * mm, "mid": v(69.78, 27.96) * mm, "end": v(69.72, 27.82) * mm});
            skLineSegment(sketch, "E1.2.0.326", {"start": v(68.47, 30.22) * mm, "end": v(68.47, 30.24) * mm});
            skLineSegment(sketch, "E1.2.0.327", {"start": v(68.47, 28.8) * mm, "end": v(68.47, 28.82) * mm});
            skArc(sketch, "E1.2.0.328", {"start": v(70.72, 27.82) * mm, "mid": v(70.66, 27.96) * mm, "end": v(70.52, 28.02) * mm});
            skArc(sketch, "E1.2.0.333", {"start": v(69.27, 28.02) * mm, "mid": v(69.41, 28.08) * mm, "end": v(69.47, 28.22) * mm});
            skArc(sketch, "E1.2.0.337", {"start": v(70.52, 29.02) * mm, "mid": v(70.66, 29.08) * mm, "end": v(70.72, 29.22) * mm});
            skLineSegment(sketch, "E1.2.0.340", {"start": v(69.72, 29.8) * mm, "end": v(69.72, 29.82) * mm});
            skLineSegment(sketch, "E1.2.0.343", {"start": v(69.57, 29.4) * mm, "end": v(69.13, 29.4) * mm});
            skLineSegment(sketch, "E1.2.0.345", {"start": v(68.47, 28.22) * mm, "end": v(68.47, 28.24) * mm});
            skLineSegment(sketch, "E1.2.0.349", {"start": v(69.47, 28.22) * mm, "end": v(69.47, 28.24) * mm});
            skArc(sketch, "E1.2.0.356", {"start": v(69.72, 29.22) * mm, "mid": v(69.78, 29.08) * mm, "end": v(69.92, 29.02) * mm});
            skLineSegment(sketch, "E1.2.0.357", {"start": v(70.72, 29.8) * mm, "end": v(70.72, 29.82) * mm});
            skArc(sketch, "E1.2.0.363", {"start": v(69.27, 30.02) * mm, "mid": v(69.41, 30.08) * mm, "end": v(69.47, 30.22) * mm});
            skLineSegment(sketch, "E1.2.0.369", {"start": v(70.52, 28.02) * mm, "end": v(69.92, 28.02) * mm});
            skArc(sketch, "E1.2.0.371", {"start": v(68.47, 30.22) * mm, "mid": v(68.53, 30.08) * mm, "end": v(68.67, 30.02) * mm});
            skArc(sketch, "E1.2.0.374", {"start": v(70.52, 27.02) * mm, "mid": v(70.66, 27.08) * mm, "end": v(70.72, 27.22) * mm});
            skLineSegment(sketch, "E1.2.0.375", {"start": v(70.52, 27.02) * mm, "end": v(69.92, 27.02) * mm});
            skLineSegment(sketch, "E1.2.0.377", {"start": v(69.57, 27.4) * mm, "end": v(69.13, 27.4) * mm});
            skLineSegment(sketch, "E1.2.0.382", {"start": v(69.57, 27.64) * mm, "end": v(69.13, 27.64) * mm});
            skArc(sketch, "E1.2.0.383", {"start": v(69.47, 28.8) * mm, "mid": v(69.52, 28.69) * mm, "end": v(69.62, 28.64) * mm});
            skLineSegment(sketch, "E1.2.0.385", {"start": v(70.72, 27.8) * mm, "end": v(70.72, 27.82) * mm});
            skArc(sketch, "E1.2.0.386", {"start": v(69.72, 27.22) * mm, "mid": v(69.78, 27.08) * mm, "end": v(69.92, 27.02) * mm});
            skArc(sketch, "E1.2.0.390", {"start": v(69.57, 27.64) * mm, "mid": v(69.68, 27.69) * mm, "end": v(69.72, 27.8) * mm});
            skArc(sketch, "E1.2.0.397", {"start": v(68.32, 28.64) * mm, "mid": v(68.43, 28.69) * mm, "end": v(68.47, 28.8) * mm});
            skArc(sketch, "E1.2.0.399", {"start": v(70.72, 27.8) * mm, "mid": v(70.77, 27.69) * mm, "end": v(70.87, 27.64) * mm});
            skLineSegment(sketch, "E1.2.0.402", {"start": v(69.47, 28.8) * mm, "end": v(69.47, 28.82) * mm});
            skArc(sketch, "E1.2.0.403", {"start": v(70.87, 29.4) * mm, "mid": v(70.77, 29.35) * mm, "end": v(70.72, 29.24) * mm});
            skArc(sketch, "E1.2.0.410", {"start": v(69.72, 29.24) * mm, "mid": v(69.68, 29.35) * mm, "end": v(69.57, 29.4) * mm});
            skArc(sketch, "E1.2.0.418", {"start": v(69.72, 27.24) * mm, "mid": v(69.68, 27.35) * mm, "end": v(69.57, 27.4) * mm});
            skArc(sketch, "E1.2.0.421", {"start": v(70.87, 27.4) * mm, "mid": v(70.77, 27.35) * mm, "end": v(70.72, 27.24) * mm});
            skLineSegment(sketch, "E1.2.0.423", {"start": v(69.72, 27.8) * mm, "end": v(69.72, 27.82) * mm});
            skLineSegment(sketch, "E1.2.0.426", {"start": v(69.47, 30.22) * mm, "end": v(69.47, 30.24) * mm});
            skLineSegment(sketch, "E1.2.0.430", {"start": v(69.72, 27.22) * mm, "end": v(69.72, 27.24) * mm});
            skLineSegment(sketch, "E1.2.0.432", {"start": v(70.72, 27.22) * mm, "end": v(70.72, 27.24) * mm});
            skPoint(sketch, "E2.4.3.0", {"position": v(79.72, 32.02) * mm});
            skPoint(sketch, "E2.5.3.0", {"position": v(80.72, 32.02) * mm});
            skPoint(sketch, "E2.8.3.0", {"position": v(80.72, 31.64) * mm});
            skPoint(sketch, "E2.10.3.0", {"position": v(78.47, 28.02) * mm});
            skPoint(sketch, "E2.13.3.0", {"position": v(80.22, 31.52) * mm});
            skPoint(sketch, "E2.16.3.0", {"position": v(79.47, 30.02) * mm});
            skPoint(sketch, "E2.17.3.0", {"position": v(78.47, 29.02) * mm});
            skPoint(sketch, "E2.19.3.0", {"position": v(79.72, 28.02) * mm});
            skPoint(sketch, "E2.22.3.0", {"position": v(78.47, 30.02) * mm});
            skPoint(sketch, "E2.23.3.0", {"position": v(80.72, 27.4) * mm});
            skPoint(sketch, "E2.24.3.0", {"position": v(78.47, 30.64) * mm});
            skPoint(sketch, "E2.34.3.0", {"position": v(80.72, 29.02) * mm});
            skPoint(sketch, "E2.35.3.0", {"position": v(78.47, 31.02) * mm});
            skPoint(sketch, "E2.36.3.0", {"position": v(80.72, 28.02) * mm});
            skPoint(sketch, "E2.37.3.0", {"position": v(79.72, 29.02) * mm});
            skPoint(sketch, "E2.40.3.0", {"position": v(79.72, 31.64) * mm});
            skPoint(sketch, "E2.41.3.0", {"position": v(80.72, 29.64) * mm});
            skPoint(sketch, "E2.45.3.0", {"position": v(80.22, 31.52) * mm});
            skPoint(sketch, "E2.46.3.0", {"position": v(80.72, 31.4) * mm});
            skPoint(sketch, "E2.51.3.0", {"position": v(78.47, 28.4) * mm});
            skPoint(sketch, "E2.54.3.0", {"position": v(78.97, 30.52) * mm});
            skPoint(sketch, "E2.59.3.0", {"position": v(78.47, 28.64) * mm});
            skPoint(sketch, "E2.69.3.0", {"position": v(79.72, 27.64) * mm});
            skPoint(sketch, "E2.70.3.0", {"position": v(78.47, 30.4) * mm});
            skPoint(sketch, "E2.71.3.0", {"position": v(79.47, 28.4) * mm});
            skPoint(sketch, "E2.73.3.0", {"position": v(80.22, 27.52) * mm});
            skPoint(sketch, "E2.74.3.0", {"position": v(79.47, 28.64) * mm});
            skPoint(sketch, "E2.80.3.0", {"position": v(79.72, 31.4) * mm});
            skPoint(sketch, "E2.82.3.0", {"position": v(80.72, 30.02) * mm});
            skPoint(sketch, "E2.84.3.0", {"position": v(80.22, 27.52) * mm});
            skPoint(sketch, "E2.85.3.0", {"position": v(80.72, 29.4) * mm});
            skPoint(sketch, "E2.87.3.0", {"position": v(80.72, 31.02) * mm});
            skPoint(sketch, "E2.90.3.0", {"position": v(78.97, 28.52) * mm});
            skPoint(sketch, "E2.92.3.0", {"position": v(78.97, 30.52) * mm});
            skPoint(sketch, "E2.94.3.0", {"position": v(80.22, 29.52) * mm});
            skPoint(sketch, "E2.96.3.0", {"position": v(80.72, 27.64) * mm});
            skPoint(sketch, "E2.108.3.0", {"position": v(79.72, 27.4) * mm});
            skPoint(sketch, "E2.112.3.0", {"position": v(79.47, 29.02) * mm});
            skPoint(sketch, "E2.115.3.0", {"position": v(80.22, 29.52) * mm});
            skPoint(sketch, "E2.119.3.0", {"position": v(79.72, 31.02) * mm});
            skPoint(sketch, "E2.128.3.0", {"position": v(79.47, 28.02) * mm});
            skPoint(sketch, "E2.136.3.0", {"position": v(78.97, 28.52) * mm});
            skPoint(sketch, "E2.143.3.0", {"position": v(79.47, 30.64) * mm});
            skPoint(sketch, "E2.149.3.0", {"position": v(79.72, 30.02) * mm});
            skPoint(sketch, "E2.150.3.0", {"position": v(79.47, 31.02) * mm});
            skPoint(sketch, "E2.156.3.0", {"position": v(79.47, 30.4) * mm});
            skPoint(sketch, "E2.157.3.0", {"position": v(79.72, 29.4) * mm});
            skPoint(sketch, "E2.158.3.0", {"position": v(79.72, 29.64) * mm});
            skLineSegment(sketch, "E2.163.3.0", {"start": v(79.13, 31.64) * mm, "end": v(77.89, 31.64) * mm});
            skLineSegment(sketch, "E2.166.3.0", {"start": v(79.13, 31.4) * mm, "end": v(77.89, 31.4) * mm});
            skLineSegment(sketch, "E2.169.3.0", {"start": v(77.89, 30.64) * mm, "end": v(78.32, 30.64) * mm});
            skLineSegment(sketch, "E2.178.3.0", {"start": v(77.89, 30.4) * mm, "end": v(78.32, 30.4) * mm});
            skLineSegment(sketch, "E2.193.3.0", {"start": v(79.13, 29.64) * mm, "end": v(77.89, 29.64) * mm});
            skLineSegment(sketch, "E2.199.3.0", {"start": v(79.13, 29.4) * mm, "end": v(77.89, 29.4) * mm});
            skLineSegment(sketch, "E2.202.3.0", {"start": v(79.13, 27.64) * mm, "end": v(77.89, 27.64) * mm});
            skArc(sketch, "E2.205.3.0", {"start": v(78.47, 28.22) * mm, "mid": v(78.53, 28.08) * mm, "end": v(78.67, 28.02) * mm});
            skLineSegment(sketch, "E2.209.3.0", {"start": v(77.89, 28.4) * mm, "end": v(78.32, 28.4) * mm});
            skLineSegment(sketch, "E2.212.3.0", {"start": v(77.89, 28.64) * mm, "end": v(78.32, 28.64) * mm});
            skLineSegment(sketch, "E2.221.3.0", {"start": v(80.52, 32.02) * mm, "end": v(79.92, 32.02) * mm});
            skLineSegment(sketch, "E2.263.3.0", {"start": v(79.13, 27.4) * mm, "end": v(77.89, 27.4) * mm});
            skArc(sketch, "E2.328.3.0", {"start": v(79.57, 31.64) * mm, "mid": v(79.68, 31.69) * mm, "end": v(79.72, 31.8) * mm});
            skArc(sketch, "E2.332.3.0", {"start": v(80.72, 31.82) * mm, "mid": v(80.66, 31.96) * mm, "end": v(80.52, 32.02) * mm});
            skLineSegment(sketch, "E2.370.3.0", {"start": v(79.72, 31.8) * mm, "end": v(79.72, 31.82) * mm});
            skLineSegment(sketch, "E2.373.3.0", {"start": v(80.72, 31.8) * mm, "end": v(80.72, 31.82) * mm});
            skArc(sketch, "E2.379.3.0", {"start": v(79.92, 32.02) * mm, "mid": v(79.78, 31.96) * mm, "end": v(79.72, 31.82) * mm});
            skLineSegment(sketch, "E2.404.3.0", {"start": v(79.27, 31.02) * mm, "end": v(78.67, 31.02) * mm});
            skLineSegment(sketch, "E2.413.3.0", {"start": v(79.57, 31.64) * mm, "end": v(79.13, 31.64) * mm});
            skArc(sketch, "E2.416.3.0", {"start": v(79.47, 30.82) * mm, "mid": v(79.41, 30.96) * mm, "end": v(79.27, 31.02) * mm});
            skArc(sketch, "E2.420.3.0", {"start": v(79.72, 31.24) * mm, "mid": v(79.68, 31.35) * mm, "end": v(79.57, 31.4) * mm});
            skLineSegment(sketch, "E2.437.3.0", {"start": v(79.57, 31.4) * mm, "end": v(79.13, 31.4) * mm});
            skLineSegment(sketch, "E2.440.3.0", {"start": v(80.52, 31.02) * mm, "end": v(79.92, 31.02) * mm});
            skArc(sketch, "E2.443.3.0", {"start": v(80.52, 31.02) * mm, "mid": v(80.66, 31.08) * mm, "end": v(80.72, 31.22) * mm});
            skLineSegment(sketch, "E2.463.3.0", {"start": v(79.72, 31.22) * mm, "end": v(79.72, 31.24) * mm});
            skLineSegment(sketch, "E2.469.3.0", {"start": v(80.72, 31.22) * mm, "end": v(80.72, 31.24) * mm});
            skArc(sketch, "E2.472.3.0", {"start": v(78.32, 30.64) * mm, "mid": v(78.43, 30.69) * mm, "end": v(78.47, 30.8) * mm});
            skArc(sketch, "E2.485.3.0", {"start": v(78.67, 31.02) * mm, "mid": v(78.53, 30.96) * mm, "end": v(78.47, 30.82) * mm});
            skLineSegment(sketch, "E2.502.3.0", {"start": v(79.47, 30.8) * mm, "end": v(79.47, 30.82) * mm});
            skArc(sketch, "E2.520.3.0", {"start": v(78.47, 30.24) * mm, "mid": v(78.43, 30.35) * mm, "end": v(78.32, 30.4) * mm});
            skArc(sketch, "E2.530.3.0", {"start": v(79.72, 31.22) * mm, "mid": v(79.78, 31.08) * mm, "end": v(79.92, 31.02) * mm});
            skLineSegment(sketch, "E2.554.3.0", {"start": v(78.47, 30.8) * mm, "end": v(78.47, 30.82) * mm});
            skLineSegment(sketch, "E2.564.3.0", {"start": v(80.52, 29.02) * mm, "end": v(79.92, 29.02) * mm});
            skArc(sketch, "E2.567.3.0", {"start": v(79.47, 28.82) * mm, "mid": v(79.41, 28.96) * mm, "end": v(79.27, 29.02) * mm});
            skLineSegment(sketch, "E2.571.3.0", {"start": v(80.52, 30.02) * mm, "end": v(79.92, 30.02) * mm});
            skLineSegment(sketch, "E2.577.3.0", {"start": v(79.27, 29.02) * mm, "end": v(78.67, 29.02) * mm});
            skLineSegment(sketch, "E2.580.3.0", {"start": v(79.27, 28.02) * mm, "end": v(78.67, 28.02) * mm});
            skLineSegment(sketch, "E2.586.3.0", {"start": v(79.57, 29.64) * mm, "end": v(79.13, 29.64) * mm});
            skArc(sketch, "E2.596.3.0", {"start": v(79.92, 30.02) * mm, "mid": v(79.78, 29.96) * mm, "end": v(79.72, 29.82) * mm});
            skArc(sketch, "E2.600.3.0", {"start": v(79.57, 29.64) * mm, "mid": v(79.68, 29.69) * mm, "end": v(79.72, 29.8) * mm});
            skArc(sketch, "E2.607.3.0", {"start": v(80.72, 29.82) * mm, "mid": v(80.66, 29.96) * mm, "end": v(80.52, 30.02) * mm});
            skArc(sketch, "E2.618.3.0", {"start": v(78.47, 28.24) * mm, "mid": v(78.43, 28.35) * mm, "end": v(78.32, 28.4) * mm});
            skArc(sketch, "E2.622.3.0", {"start": v(78.67, 29.02) * mm, "mid": v(78.53, 28.96) * mm, "end": v(78.47, 28.82) * mm});
            skLineSegment(sketch, "E2.645.3.0", {"start": v(79.27, 30.02) * mm, "end": v(78.67, 30.02) * mm});
            skLineSegment(sketch, "E2.648.3.0", {"start": v(79.72, 29.22) * mm, "end": v(79.72, 29.24) * mm});
            skLineSegment(sketch, "E2.658.3.0", {"start": v(80.72, 29.22) * mm, "end": v(80.72, 29.24) * mm});
            skArc(sketch, "E2.665.3.0", {"start": v(79.92, 28.02) * mm, "mid": v(79.78, 27.96) * mm, "end": v(79.72, 27.82) * mm});
            skLineSegment(sketch, "E2.693.3.0", {"start": v(78.47, 30.22) * mm, "end": v(78.47, 30.24) * mm});
            skLineSegment(sketch, "E2.696.3.0", {"start": v(78.47, 28.8) * mm, "end": v(78.47, 28.82) * mm});
            skArc(sketch, "E2.699.3.0", {"start": v(80.72, 27.82) * mm, "mid": v(80.66, 27.96) * mm, "end": v(80.52, 28.02) * mm});
            skArc(sketch, "E2.715.3.0", {"start": v(79.27, 28.02) * mm, "mid": v(79.41, 28.08) * mm, "end": v(79.47, 28.22) * mm});
            skArc(sketch, "E2.730.3.0", {"start": v(80.52, 29.02) * mm, "mid": v(80.66, 29.08) * mm, "end": v(80.72, 29.22) * mm});
            skLineSegment(sketch, "E2.742.3.0", {"start": v(79.72, 29.8) * mm, "end": v(79.72, 29.82) * mm});
            skLineSegment(sketch, "E2.751.3.0", {"start": v(79.57, 29.4) * mm, "end": v(79.13, 29.4) * mm});
            skLineSegment(sketch, "E2.758.3.0", {"start": v(78.47, 28.22) * mm, "end": v(78.47, 28.24) * mm});
            skLineSegment(sketch, "E2.773.3.0", {"start": v(79.47, 28.22) * mm, "end": v(79.47, 28.24) * mm});
            skArc(sketch, "E2.799.3.0", {"start": v(79.72, 29.22) * mm, "mid": v(79.78, 29.08) * mm, "end": v(79.92, 29.02) * mm});
            skLineSegment(sketch, "E2.803.3.0", {"start": v(80.72, 29.8) * mm, "end": v(80.72, 29.82) * mm});
            skArc(sketch, "E2.825.3.0", {"start": v(79.27, 30.02) * mm, "mid": v(79.41, 30.08) * mm, "end": v(79.47, 30.22) * mm});
            skLineSegment(sketch, "E2.848.3.0", {"start": v(80.52, 28.02) * mm, "end": v(79.92, 28.02) * mm});
            skArc(sketch, "E2.855.3.0", {"start": v(78.47, 30.22) * mm, "mid": v(78.53, 30.08) * mm, "end": v(78.67, 30.02) * mm});
            skArc(sketch, "E2.866.3.0", {"start": v(80.52, 27.02) * mm, "mid": v(80.66, 27.08) * mm, "end": v(80.72, 27.22) * mm});
            skLineSegment(sketch, "E2.870.3.0", {"start": v(80.52, 27.02) * mm, "end": v(79.92, 27.02) * mm});
            skLineSegment(sketch, "E2.877.3.0", {"start": v(79.57, 27.4) * mm, "end": v(79.13, 27.4) * mm});
            skLineSegment(sketch, "E2.894.3.0", {"start": v(79.57, 27.64) * mm, "end": v(79.13, 27.64) * mm});
            skLineSegment(sketch, "E2.904.3.0", {"start": v(80.72, 27.8) * mm, "end": v(80.72, 27.82) * mm});
            skArc(sketch, "E2.907.3.0", {"start": v(79.72, 27.22) * mm, "mid": v(79.78, 27.08) * mm, "end": v(79.92, 27.02) * mm});
            skArc(sketch, "E2.922.3.0", {"start": v(79.57, 27.64) * mm, "mid": v(79.68, 27.69) * mm, "end": v(79.72, 27.8) * mm});
            skArc(sketch, "E2.947.3.0", {"start": v(78.32, 28.64) * mm, "mid": v(78.43, 28.69) * mm, "end": v(78.47, 28.8) * mm});
            skLineSegment(sketch, "E2.965.3.0", {"start": v(79.47, 28.8) * mm, "end": v(79.47, 28.82) * mm});
            skArc(sketch, "E2.992.3.0", {"start": v(79.72, 29.24) * mm, "mid": v(79.68, 29.35) * mm, "end": v(79.57, 29.4) * mm});
            skArc(sketch, "E2.1020.3.0", {"start": v(79.72, 27.24) * mm, "mid": v(79.68, 27.35) * mm, "end": v(79.57, 27.4) * mm});
            skLineSegment(sketch, "E2.1038.3.0", {"start": v(79.72, 27.8) * mm, "end": v(79.72, 27.82) * mm});
            skLineSegment(sketch, "E2.1049.3.0", {"start": v(79.47, 30.22) * mm, "end": v(79.47, 30.24) * mm});
            skLineSegment(sketch, "E2.1063.3.0", {"start": v(79.72, 27.22) * mm, "end": v(79.72, 27.24) * mm});
            skLineSegment(sketch, "E2.1070.3.0", {"start": v(80.72, 27.22) * mm, "end": v(80.72, 27.24) * mm});
            skLineSegment(sketch, "E3", {"start": v(71.17, 31.64) * mm, "end": v(77.89, 31.64) * mm});
            skLineSegment(sketch, "E4", {"start": v(71.17, 31.4) * mm, "end": v(77.89, 31.4) * mm});
            skLineSegment(sketch, "E5", {"start": v(71.17, 30.64) * mm, "end": v(77.89, 30.64) * mm});
            skLineSegment(sketch, "E6", {"start": v(71.17, 30.4) * mm, "end": v(77.89, 30.4) * mm});
            skLineSegment(sketch, "E7", {"start": v(80.72, 31.8) * mm, "end": v(80.72, 31.24) * mm});
            skLineSegment(sketch, "E8", {"start": v(79.47, 30.8) * mm, "end": v(79.47, 30.24) * mm});
            skLineSegment(sketch, "E9", {"start": v(80.72, 29.8) * mm, "end": v(80.72, 29.24) * mm});
            skLineSegment(sketch, "E10", {"start": v(79.47, 28.8) * mm, "end": v(79.47, 28.24) * mm});
            skLineSegment(sketch, "E11", {"start": v(80.72, 27.8) * mm, "end": v(80.72, 27.24) * mm});
            skLineSegment(sketch, "E12", {"start": v(71.17, 29.64) * mm, "end": v(77.89, 29.64) * mm});
            skLineSegment(sketch, "E13", {"start": v(77.89, 29.4) * mm, "end": v(71.17, 29.4) * mm});
            skLineSegment(sketch, "E14", {"start": v(71.17, 28.64) * mm, "end": v(77.89, 28.64) * mm});
            skLineSegment(sketch, "E15", {"start": v(77.89, 28.4) * mm, "end": v(71.17, 28.4) * mm});
            skLineSegment(sketch, "E16", {"start": v(71.17, 27.64) * mm, "end": v(77.89, 27.64) * mm});
            skLineSegment(sketch, "E17", {"start": v(77.89, 27.4) * mm, "end": v(71.17, 27.4) * mm});
            skLineSegment(sketch, "E18", {"start": v(67.89, 31.64) * mm, "end": v(61.17, 31.64) * mm});
            skLineSegment(sketch, "E19", {"start": v(67.89, 31.4) * mm, "end": v(61.17, 31.4) * mm});
            skLineSegment(sketch, "E20", {"start": v(67.89, 30.64) * mm, "end": v(61.17, 30.64) * mm});
            skLineSegment(sketch, "E21", {"start": v(67.89, 30.4) * mm, "end": v(61.17, 30.4) * mm});
            skLineSegment(sketch, "E22", {"start": v(67.89, 29.64) * mm, "end": v(61.17, 29.64) * mm});
            skLineSegment(sketch, "E23", {"start": v(67.89, 29.4) * mm, "end": v(61.17, 29.4) * mm});
            skLineSegment(sketch, "E24", {"start": v(67.89, 28.64) * mm, "end": v(61.17, 28.64) * mm});
            skLineSegment(sketch, "E25", {"start": v(67.89, 28.4) * mm, "end": v(61.17, 28.4) * mm});
            skLineSegment(sketch, "E26", {"start": v(67.89, 27.64) * mm, "end": v(61.17, 27.64) * mm});
            skLineSegment(sketch, "E27", {"start": v(67.89, 27.4) * mm, "end": v(61.17, 27.4) * mm});
            skLineSegment(sketch, "E28", {"start": v(51.17, 31.64) * mm, "end": v(57.89, 31.64) * mm});
            skLineSegment(sketch, "E29", {"start": v(57.89, 31.4) * mm, "end": v(51.17, 31.4) * mm});
            skLineSegment(sketch, "E30", {"start": v(51.17, 30.64) * mm, "end": v(57.89, 30.64) * mm});
            skLineSegment(sketch, "E31", {"start": v(57.89, 30.4) * mm, "end": v(51.17, 30.4) * mm});
            skLineSegment(sketch, "E32", {"start": v(51.17, 29.64) * mm, "end": v(57.89, 29.64) * mm});
            skLineSegment(sketch, "E33", {"start": v(57.89, 29.4) * mm, "end": v(51.17, 29.4) * mm});
            skLineSegment(sketch, "E34", {"start": v(57.89, 28.64) * mm, "end": v(51.17, 28.64) * mm});
            skLineSegment(sketch, "E35", {"start": v(57.89, 28.4) * mm, "end": v(51.17, 28.4) * mm});
            skLineSegment(sketch, "E36", {"start": v(57.89, 27.64) * mm, "end": v(51.17, 27.64) * mm});
            skLineSegment(sketch, "E37", {"start": v(57.89, 27.4) * mm, "end": v(51.17, 27.4) * mm});
            skLineSegment(sketch, "E38", {"start": v(47.89, 30.64) * mm, "end": v(46.76, 30.64) * mm});
            skLineSegment(sketch, "E39", {"start": v(47.89, 30.4) * mm, "end": v(46.76, 30.4) * mm});
            skLineSegment(sketch, "E40", {"start": v(47.89, 28.64) * mm, "end": v(46.76, 28.64) * mm});
            skLineSegment(sketch, "E41", {"start": v(47.89, 28.4) * mm, "end": v(46.76, 28.4) * mm});
            skLineSegment(sketch, "E42", {"start": v(47.89, 31.64) * mm, "end": v(43.7, 31.64) * mm});
            skLineSegment(sketch, "E43", {"start": v(47.89, 27.4) * mm, "end": v(43.7, 27.4) * mm});
            skLineSegment(sketch, "E44", {"start": v(46.64, 30.77) * mm, "end": v(46.64, 31.26) * mm});
            skLineSegment(sketch, "E45", {"start": v(46.64, 30.26) * mm, "end": v(46.64, 29.77) * mm});
            skLineSegment(sketch, "E46", {"start": v(46.64, 28.26) * mm, "end": v(46.64, 27.77) * mm});
            skLineSegment(sketch, "E47", {"start": v(47.89, 27.64) * mm, "end": v(46.76, 27.64) * mm});
            skLineSegment(sketch, "E48", {"start": v(47.89, 29.4) * mm, "end": v(46.76, 29.4) * mm});
            skLineSegment(sketch, "E49", {"start": v(46.76, 29.64) * mm, "end": v(47.89, 29.64) * mm});
            skLineSegment(sketch, "E50", {"start": v(47.89, 31.4) * mm, "end": v(46.76, 31.4) * mm});
            skLineSegment(sketch, "E51", {"start": v(42.62, 28.46) * mm, "end": v(42.62, 30.58) * mm});
            skPoint(sketch, "E52.visualSharp", {"position": v(42.62, 31.64) * mm});
            skArc(sketch, "E52.filletArc", {"start": v(43.7, 31.64) * mm, "mid": v(42.94, 31.33) * mm, "end": v(42.62, 30.58) * mm});
            skPoint(sketch, "E53.visualSharp", {"position": v(42.62, 27.4) * mm});
            skArc(sketch, "E53.filletArc", {"start": v(42.62, 28.46) * mm, "mid": v(42.94, 27.7) * mm, "end": v(43.7, 27.4) * mm});
            skPoint(sketch, "E54.visualSharp", {"position": v(46.64, 31.4) * mm});
            skArc(sketch, "E54.filletArc", {"start": v(46.76, 31.4) * mm, "mid": v(46.67, 31.35) * mm, "end": v(46.64, 31.26) * mm});
            skPoint(sketch, "E55.visualSharp", {"position": v(46.64, 30.64) * mm});
            skArc(sketch, "E55.filletArc", {"start": v(46.64, 30.77) * mm, "mid": v(46.67, 30.68) * mm, "end": v(46.76, 30.64) * mm});
            skPoint(sketch, "E56.visualSharp", {"position": v(46.64, 30.4) * mm});
            skArc(sketch, "E56.filletArc", {"start": v(46.76, 30.4) * mm, "mid": v(46.67, 30.35) * mm, "end": v(46.64, 30.26) * mm});
            skPoint(sketch, "E57.visualSharp", {"position": v(46.64, 28.64) * mm});
            skArc(sketch, "E57.filletArc", {"start": v(46.64, 28.77) * mm, "mid": v(46.67, 28.68) * mm, "end": v(46.76, 28.64) * mm});
            skPoint(sketch, "E58.visualSharp", {"position": v(46.64, 28.4) * mm});
            skArc(sketch, "E58.filletArc", {"start": v(46.76, 28.4) * mm, "mid": v(46.67, 28.35) * mm, "end": v(46.64, 28.26) * mm});
            skPoint(sketch, "E59.visualSharp", {"position": v(46.64, 27.64) * mm});
            skArc(sketch, "E59.filletArc", {"start": v(46.64, 27.77) * mm, "mid": v(46.67, 27.68) * mm, "end": v(46.76, 27.64) * mm});
            skLineSegment(sketch, "E60.trimOffspring", {"start": v(46.64, 29.26) * mm, "end": v(46.64, 28.77) * mm});
            skPoint(sketch, "E61.visualSharp", {"position": v(46.64, 29.64) * mm});
            skArc(sketch, "E61.filletArc", {"start": v(46.64, 29.77) * mm, "mid": v(46.67, 29.68) * mm, "end": v(46.76, 29.64) * mm});
            skPoint(sketch, "E62.visualSharp", {"position": v(46.64, 29.4) * mm});
            skArc(sketch, "E62.filletArc", {"start": v(46.76, 29.4) * mm, "mid": v(46.67, 29.35) * mm, "end": v(46.64, 29.26) * mm});
            skSolve(sketch);
        }
        {
            var Q0;
            Q0=makeQuery(id+"F0.imprint","IMPRINT",FACE,{"disambiguationData":[TD([[makeQuery(id+"F0.imprint","IMPRINT",EDGE,{"derivedFrom":sQuery(id+"F0.wireOp",EDGE,"E0.0.5.4")}),1.0]])]});
            extrude(context, id + "F1", {"entities" : qUnion([Q0]), "depth" : .25 * mm, "offsetDistance" : 25 * mm});
        }
        {
            var Q0;
            Q0=qCreatedBy(makeId("Front.planeOp"),FACE);
            var sketch = newSketch(context, id + "F2", { "sketchPlane" : qUnion([Q0])});
            skLineSegment(sketch, "E63.bottom", {"start": v(81.1, 29) * mm, "end": v(81.15, 29) * mm});
            skLineSegment(sketch, "E63.top", {"start": v(81.1, 30) * mm, "end": v(81.15, 30) * mm});
            skLineSegment(sketch, "E63.left", {"start": v(81.1, 29) * mm, "end": v(81.1, 30) * mm});
            skLineSegment(sketch, "E63.right", {"start": v(81.15, 29) * mm, "end": v(81.15, 30) * mm});
            skLineSegment(sketch, "E64.bottom", {"start": v(81.1, 30) * mm, "end": v(81.31, 30) * mm});
            skLineSegment(sketch, "E64.top", {"start": v(81.1, 29.97) * mm, "end": v(81.31, 29.97) * mm});
            skLineSegment(sketch, "E64.left", {"start": v(81.1, 30) * mm, "end": v(81.1, 29.97) * mm});
            skLineSegment(sketch, "E64.right", {"start": v(81.31, 30) * mm, "end": v(81.31, 29.97) * mm});
            skLineSegment(sketch, "E65.bottom", {"start": v(81.1, 29) * mm, "end": v(81.31, 29) * mm});
            skLineSegment(sketch, "E65.top", {"start": v(81.1, 29.05) * mm, "end": v(81.31, 29.05) * mm});
            skLineSegment(sketch, "E65.left", {"start": v(81.1, 29) * mm, "end": v(81.1, 29.05) * mm});
            skLineSegment(sketch, "E65.right", {"start": v(81.31, 29) * mm, "end": v(81.31, 29.05) * mm});
            skText(sketch, "E66", { "text": "1 mm", "fontName": "OpenSans-Regular.ttf"});
            const initialGuessF2  = {"E66": [0.08135, 0.02935, 1, 0, 0.00035]};
            skSetInitialGuess(sketch, initialGuessF2);
            skSolve(sketch);
        }
        {
            var Q0;
            Q0 = qSketchRegion(id + "F2", true);
            extrude(context, id + "F3", {"entities" : qUnion([Q0]), "depth" : .25 * mm, "offsetDistance" : 25 * mm});
        }
        {
            var Q0;
            Q0=makeQuery(id+"F1.opExtrude","CAP_FACE",FACE,{"disambiguationData":[OSD([sQuery(id+"F0.wireOp",EDGE,"E0.0.5.4"),sQuery(id+"F0.wireOp",EDGE,"E0.0.5.5"),sQuery(id+"F0.wireOp",EDGE,"E0.0.5.6"),sQuery(id+"F0.wireOp",EDGE,"E0.0.5.7"),sQuery(id+"F0.wireOp",EDGE,"E0.0.5.18"),sQuery(id+"F0.wireOp",EDGE,"E0.0.5.19"),sQuery(id+"F0.wireOp",EDGE,"E0.0.5.32"),sQuery(id+"F0.wireOp",EDGE,"E0.0.5.33"),sQuery(id+"F0.wireOp",EDGE,"E0.0.5.34"),sQuery(id+"F0.wireOp",EDGE,"E0.0.5.41"),sQuery(id+"F0.wireOp",EDGE,"E0.0.5.44"),sQuery(id+"F0.wireOp",EDGE,"E0.0.5.45"),sQuery(id+"F0.wireOp",EDGE,"E0.0.5.46"),sQuery(id+"F0.wireOp",EDGE,"E0.0.5.49"),sQuery(id+"F0.wireOp",EDGE,"E0.0.5.50"),sQuery(id+"F0.wireOp",EDGE,"E0.0.5.55"),sQuery(id+"F0.wireOp",EDGE,"E0.0.5.56"),sQuery(id+"F0.wireOp",EDGE,"E0.0.5.57"),sQuery(id+"F0.wireOp",EDGE,"E0.0.5.60"),sQuery(id+"F0.wireOp",EDGE,"E0.0.5.61"),sQuery(id+"F0.wireOp",EDGE,"E0.0.6.0"),sQuery(id+"F0.wireOp",EDGE,"E0.0.6.1"),sQuery(id+"F0.wireOp",EDGE,"E0.0.6.2"),sQuery(id+"F0.wireOp",EDGE,"E0.0.6.3"),sQuery(id+"F0.wireOp",EDGE,"E0.0.6.4"),sQuery(id+"F0.wireOp",EDGE,"E0.0.6.5"),sQuery(id+"F0.wireOp",EDGE,"E0.0.6.6"),sQuery(id+"F0.wireOp",EDGE,"E0.0.6.7"),sQuery(id+"F0.wireOp",EDGE,"E0.0.6.18"),sQuery(id+"F0.wireOp",EDGE,"E0.0.6.19"),sQuery(id+"F0.wireOp",EDGE,"E0.0.6.22"),sQuery(id+"F0.wireOp",EDGE,"E0.0.6.25"),sQuery(id+"F0.wireOp",EDGE,"E0.0.6.32"),sQuery(id+"F0.wireOp",EDGE,"E0.0.6.33"),sQuery(id+"F0.wireOp",EDGE,"E0.0.6.34"),sQuery(id+"F0.wireOp",EDGE,"E0.0.6.35"),sQuery(id+"F0.wireOp",EDGE,"E0.0.6.36"),sQuery(id+"F0.wireOp",EDGE,"E0.0.6.37"),sQuery(id+"F0.wireOp",EDGE,"E0.0.6.39"),sQuery(id+"F0.wireOp",EDGE,"E0.0.6.41"),sQuery(id+"F0.wireOp",EDGE,"E0.0.6.44"),sQuery(id+"F0.wireOp",EDGE,"E0.0.6.45"),sQuery(id+"F0.wireOp",EDGE,"E0.0.6.46"),sQuery(id+"F0.wireOp",EDGE,"E0.0.6.47"),sQuery(id+"F0.wireOp",EDGE,"E0.0.6.48"),sQuery(id+"F0.wireOp",EDGE,"E0.0.6.49"),sQuery(id+"F0.wireOp",EDGE,"E0.0.6.50"),sQuery(id+"F0.wireOp",EDGE,"E0.0.6.51"),sQuery(id+"F0.wireOp",EDGE,"E0.0.6.52"),sQuery(id+"F0.wireOp",EDGE,"E0.0.6.53"),sQuery(id+"F0.wireOp",EDGE,"E0.0.6.54"),sQuery(id+"F0.wireOp",EDGE,"E0.0.6.55"),sQuery(id+"F0.wireOp",EDGE,"E0.0.6.56"),sQuery(id+"F0.wireOp",EDGE,"E0.0.6.57"),sQuery(id+"F0.wireOp",EDGE,"E0.0.6.58"),sQuery(id+"F0.wireOp",EDGE,"E0.0.6.59"),sQuery(id+"F0.wireOp",EDGE,"E0.0.6.60"),sQuery(id+"F0.wireOp",EDGE,"E0.0.6.61"),sQuery(id+"F0.wireOp",EDGE,"E0.0.7.0"),sQuery(id+"F0.wireOp",EDGE,"E0.0.7.1"),sQuery(id+"F0.wireOp",EDGE,"E0.0.7.2"),sQuery(id+"F0.wireOp",EDGE,"E0.0.7.3"),sQuery(id+"F0.wireOp",EDGE,"E0.0.7.4"),sQuery(id+"F0.wireOp",EDGE,"E0.0.7.5"),sQuery(id+"F0.wireOp",EDGE,"E0.0.7.6"),sQuery(id+"F0.wireOp",EDGE,"E0.0.7.7"),sQuery(id+"F0.wireOp",EDGE,"E0.0.7.18"),sQuery(id+"F0.wireOp",EDGE,"E0.0.7.19"),sQuery(id+"F0.wireOp",EDGE,"E0.0.7.22"),sQuery(id+"F0.wireOp",EDGE,"E0.0.7.25"),sQuery(id+"F0.wireOp",EDGE,"E0.0.7.32"),sQuery(id+"F0.wireOp",EDGE,"E0.0.7.33"),sQuery(id+"F0.wireOp",EDGE,"E0.0.7.34"),sQuery(id+"F0.wireOp",EDGE,"E0.0.7.35"),sQuery(id+"F0.wireOp",EDGE,"E0.0.7.36"),sQuery(id+"F0.wireOp",EDGE,"E0.0.7.37"),sQuery(id+"F0.wireOp",EDGE,"E0.0.7.39"),sQuery(id+"F0.wireOp",EDGE,"E0.0.7.41"),sQuery(id+"F0.wireOp",EDGE,"E0.0.7.44"),sQuery(id+"F0.wireOp",EDGE,"E0.0.7.45"),sQuery(id+"F0.wireOp",EDGE,"E0.0.7.46"),sQuery(id+"F0.wireOp",EDGE,"E0.0.7.47"),sQuery(id+"F0.wireOp",EDGE,"E0.0.7.48"),sQuery(id+"F0.wireOp",EDGE,"E0.0.7.49"),sQuery(id+"F0.wireOp",EDGE,"E0.0.7.50"),sQuery(id+"F0.wireOp",EDGE,"E0.0.7.51"),sQuery(id+"F0.wireOp",EDGE,"E0.0.7.52"),sQuery(id+"F0.wireOp",EDGE,"E0.0.7.53"),sQuery(id+"F0.wireOp",EDGE,"E0.0.7.54"),sQuery(id+"F0.wireOp",EDGE,"E0.0.7.55"),sQuery(id+"F0.wireOp",EDGE,"E0.0.7.56"),sQuery(id+"F0.wireOp",EDGE,"E0.0.7.57"),sQuery(id+"F0.wireOp",EDGE,"E0.0.7.58"),sQuery(id+"F0.wireOp",EDGE,"E0.0.7.59"),sQuery(id+"F0.wireOp",EDGE,"E0.0.7.60"),sQuery(id+"F0.wireOp",EDGE,"E0.0.7.61"),sQuery(id+"F0.wireOp",EDGE,"E1.1.0.161"),sQuery(id+"F0.wireOp",EDGE,"E1.1.0.162"),sQuery(id+"F0.wireOp",EDGE,"E1.1.0.163"),sQuery(id+"F0.wireOp",EDGE,"E1.1.0.166"),sQuery(id+"F0.wireOp",EDGE,"E1.1.0.171"),sQuery(id+"F0.wireOp",EDGE,"E1.1.0.173"),sQuery(id+"F0.wireOp",EDGE,"E1.1.0.174"),sQuery(id+"F0.wireOp",EDGE,"E1.1.0.175"),sQuery(id+"F0.wireOp",EDGE,"E1.1.0.176"),sQuery(id+"F0.wireOp",EDGE,"E1.1.0.177"),sQuery(id+"F0.wireOp",EDGE,"E1.1.0.180"),sQuery(id+"F0.wireOp",EDGE,"E1.1.0.185"),sQuery(id+"F0.wireOp",EDGE,"E1.1.0.194"),sQuery(id+"F0.wireOp",EDGE,"E1.1.0.205"),sQuery(id+"F0.wireOp",EDGE,"E1.1.0.215"),sQuery(id+"F0.wireOp",EDGE,"E1.1.0.216"),sQuery(id+"F0.wireOp",EDGE,"E1.1.0.218"),sQuery(id+"F0.wireOp",EDGE,"E1.1.0.222"),sQuery(id+"F0.wireOp",EDGE,"E1.1.0.228"),sQuery(id+"F0.wireOp",EDGE,"E1.1.0.229"),sQuery(id+"F0.wireOp",EDGE,"E1.1.0.230"),sQuery(id+"F0.wireOp",EDGE,"E1.1.0.231"),sQuery(id+"F0.wireOp",EDGE,"E1.1.0.239"),sQuery(id+"F0.wireOp",EDGE,"E1.1.0.240"),sQuery(id+"F0.wireOp",EDGE,"E1.1.0.242"),sQuery(id+"F0.wireOp",EDGE,"E1.1.0.243"),sQuery(id+"F0.wireOp",EDGE,"E1.1.0.244"),sQuery(id+"F0.wireOp",EDGE,"E1.1.0.246"),sQuery(id+"F0.wireOp",EDGE,"E1.1.0.249"),sQuery(id+"F0.wireOp",EDGE,"E1.1.0.250"),sQuery(id+"F0.wireOp",EDGE,"E1.1.0.251"),sQuery(id+"F0.wireOp",EDGE,"E1.1.0.253"),sQuery(id+"F0.wireOp",EDGE,"E1.1.0.257"),sQuery(id+"F0.wireOp",EDGE,"E1.1.0.259"),sQuery(id+"F0.wireOp",EDGE,"E1.1.0.260"),sQuery(id+"F0.wireOp",EDGE,"E1.1.0.264"),sQuery(id+"F0.wireOp",EDGE,"E1.1.0.265"),sQuery(id+"F0.wireOp",EDGE,"E1.1.0.266"),sQuery(id+"F0.wireOp",EDGE,"E1.1.0.269"),sQuery(id+"F0.wireOp",EDGE,"E1.1.0.274"),sQuery(id+"F0.wireOp",EDGE,"E1.1.0.275"),sQuery(id+"F0.wireOp",EDGE,"E1.1.0.276"),sQuery(id+"F0.wireOp",EDGE,"E1.1.0.278"),sQuery(id+"F0.wireOp",EDGE,"E1.1.0.280"),sQuery(id+"F0.wireOp",EDGE,"E1.1.0.284"),sQuery(id+"F0.wireOp",EDGE,"E1.1.0.285"),sQuery(id+"F0.wireOp",EDGE,"E1.1.0.288"),sQuery(id+"F0.wireOp",EDGE,"E1.1.0.289"),sQuery(id+"F0.wireOp",EDGE,"E1.1.0.290"),sQuery(id+"F0.wireOp",EDGE,"E1.1.0.292"),sQuery(id+"F0.wireOp",EDGE,"E1.1.0.293"),sQuery(id+"F0.wireOp",EDGE,"E1.1.0.295"),sQuery(id+"F0.wireOp",EDGE,"E1.1.0.298"),sQuery(id+"F0.wireOp",EDGE,"E1.1.0.299"),sQuery(id+"F0.wireOp",EDGE,"E1.1.0.301"),sQuery(id+"F0.wireOp",EDGE,"E1.1.0.304"),sQuery(id+"F0.wireOp",EDGE,"E1.1.0.305"),sQuery(id+"F0.wireOp",EDGE,"E1.1.0.308"),sQuery(id+"F0.wireOp",EDGE,"E1.1.0.311"),sQuery(id+"F0.wireOp",EDGE,"E1.1.0.312"),sQuery(id+"F0.wireOp",EDGE,"E1.1.0.315"),sQuery(id+"F0.wireOp",EDGE,"E1.1.0.316"),sQuery(id+"F0.wireOp",EDGE,"E1.1.0.317"),sQuery(id+"F0.wireOp",EDGE,"E1.1.0.326"),sQuery(id+"F0.wireOp",EDGE,"E1.1.0.327"),sQuery(id+"F0.wireOp",EDGE,"E1.1.0.328"),sQuery(id+"F0.wireOp",EDGE,"E1.1.0.333"),sQuery(id+"F0.wireOp",EDGE,"E1.1.0.337"),sQuery(id+"F0.wireOp",EDGE,"E1.1.0.340"),sQuery(id+"F0.wireOp",EDGE,"E1.1.0.343"),sQuery(id+"F0.wireOp",EDGE,"E1.1.0.345"),sQuery(id+"F0.wireOp",EDGE,"E1.1.0.349"),sQuery(id+"F0.wireOp",EDGE,"E1.1.0.356"),sQuery(id+"F0.wireOp",EDGE,"E1.1.0.357"),sQuery(id+"F0.wireOp",EDGE,"E1.1.0.363"),sQuery(id+"F0.wireOp",EDGE,"E1.1.0.369"),sQuery(id+"F0.wireOp",EDGE,"E1.1.0.371"),sQuery(id+"F0.wireOp",EDGE,"E1.1.0.374"),sQuery(id+"F0.wireOp",EDGE,"E1.1.0.375"),sQuery(id+"F0.wireOp",EDGE,"E1.1.0.377"),sQuery(id+"F0.wireOp",EDGE,"E1.1.0.382"),sQuery(id+"F0.wireOp",EDGE,"E1.1.0.383"),sQuery(id+"F0.wireOp",EDGE,"E1.1.0.385"),sQuery(id+"F0.wireOp",EDGE,"E1.1.0.386"),sQuery(id+"F0.wireOp",EDGE,"E1.1.0.390"),sQuery(id+"F0.wireOp",EDGE,"E1.1.0.397"),sQuery(id+"F0.wireOp",EDGE,"E1.1.0.399"),sQuery(id+"F0.wireOp",EDGE,"E1.1.0.402"),sQuery(id+"F0.wireOp",EDGE,"E1.1.0.403"),sQuery(id+"F0.wireOp",EDGE,"E1.1.0.410"),sQuery(id+"F0.wireOp",EDGE,"E1.1.0.418"),sQuery(id+"F0.wireOp",EDGE,"E1.1.0.421"),sQuery(id+"F0.wireOp",EDGE,"E1.1.0.423"),sQuery(id+"F0.wireOp",EDGE,"E1.1.0.426"),sQuery(id+"F0.wireOp",EDGE,"E1.1.0.430"),sQuery(id+"F0.wireOp",EDGE,"E1.1.0.432"),sQuery(id+"F0.wireOp",EDGE,"E1.2.0.161"),sQuery(id+"F0.wireOp",EDGE,"E1.2.0.162"),sQuery(id+"F0.wireOp",EDGE,"E1.2.0.163"),sQuery(id+"F0.wireOp",EDGE,"E1.2.0.166"),sQuery(id+"F0.wireOp",EDGE,"E1.2.0.171"),sQuery(id+"F0.wireOp",EDGE,"E1.2.0.173"),sQuery(id+"F0.wireOp",EDGE,"E1.2.0.174"),sQuery(id+"F0.wireOp",EDGE,"E1.2.0.175"),sQuery(id+"F0.wireOp",EDGE,"E1.2.0.176"),sQuery(id+"F0.wireOp",EDGE,"E1.2.0.177"),sQuery(id+"F0.wireOp",EDGE,"E1.2.0.180"),sQuery(id+"F0.wireOp",EDGE,"E1.2.0.185"),sQuery(id+"F0.wireOp",EDGE,"E1.2.0.194"),sQuery(id+"F0.wireOp",EDGE,"E1.2.0.205"),sQuery(id+"F0.wireOp",EDGE,"E1.2.0.215"),sQuery(id+"F0.wireOp",EDGE,"E1.2.0.216"),sQuery(id+"F0.wireOp",EDGE,"E1.2.0.218"),sQuery(id+"F0.wireOp",EDGE,"E1.2.0.222"),sQuery(id+"F0.wireOp",EDGE,"E1.2.0.228"),sQuery(id+"F0.wireOp",EDGE,"E1.2.0.229"),sQuery(id+"F0.wireOp",EDGE,"E1.2.0.230"),sQuery(id+"F0.wireOp",EDGE,"E1.2.0.231"),sQuery(id+"F0.wireOp",EDGE,"E1.2.0.239"),sQuery(id+"F0.wireOp",EDGE,"E1.2.0.240"),sQuery(id+"F0.wireOp",EDGE,"E1.2.0.242"),sQuery(id+"F0.wireOp",EDGE,"E1.2.0.243"),sQuery(id+"F0.wireOp",EDGE,"E1.2.0.244"),sQuery(id+"F0.wireOp",EDGE,"E1.2.0.246"),sQuery(id+"F0.wireOp",EDGE,"E1.2.0.249"),sQuery(id+"F0.wireOp",EDGE,"E1.2.0.250"),sQuery(id+"F0.wireOp",EDGE,"E1.2.0.251"),sQuery(id+"F0.wireOp",EDGE,"E1.2.0.253"),sQuery(id+"F0.wireOp",EDGE,"E1.2.0.257"),sQuery(id+"F0.wireOp",EDGE,"E1.2.0.259"),sQuery(id+"F0.wireOp",EDGE,"E1.2.0.260"),sQuery(id+"F0.wireOp",EDGE,"E1.2.0.264"),sQuery(id+"F0.wireOp",EDGE,"E1.2.0.265"),sQuery(id+"F0.wireOp",EDGE,"E1.2.0.266"),sQuery(id+"F0.wireOp",EDGE,"E1.2.0.269"),sQuery(id+"F0.wireOp",EDGE,"E1.2.0.274"),sQuery(id+"F0.wireOp",EDGE,"E1.2.0.275"),sQuery(id+"F0.wireOp",EDGE,"E1.2.0.276"),sQuery(id+"F0.wireOp",EDGE,"E1.2.0.278"),sQuery(id+"F0.wireOp",EDGE,"E1.2.0.280"),sQuery(id+"F0.wireOp",EDGE,"E1.2.0.284"),sQuery(id+"F0.wireOp",EDGE,"E1.2.0.285"),sQuery(id+"F0.wireOp",EDGE,"E1.2.0.288"),sQuery(id+"F0.wireOp",EDGE,"E1.2.0.289"),sQuery(id+"F0.wireOp",EDGE,"E1.2.0.290"),sQuery(id+"F0.wireOp",EDGE,"E1.2.0.292"),sQuery(id+"F0.wireOp",EDGE,"E1.2.0.293"),sQuery(id+"F0.wireOp",EDGE,"E1.2.0.295"),sQuery(id+"F0.wireOp",EDGE,"E1.2.0.298"),sQuery(id+"F0.wireOp",EDGE,"E1.2.0.299"),sQuery(id+"F0.wireOp",EDGE,"E1.2.0.301"),sQuery(id+"F0.wireOp",EDGE,"E1.2.0.304"),sQuery(id+"F0.wireOp",EDGE,"E1.2.0.305"),sQuery(id+"F0.wireOp",EDGE,"E1.2.0.308"),sQuery(id+"F0.wireOp",EDGE,"E1.2.0.311"),sQuery(id+"F0.wireOp",EDGE,"E1.2.0.312"),sQuery(id+"F0.wireOp",EDGE,"E1.2.0.315"),sQuery(id+"F0.wireOp",EDGE,"E1.2.0.316"),sQuery(id+"F0.wireOp",EDGE,"E1.2.0.317"),sQuery(id+"F0.wireOp",EDGE,"E1.2.0.326"),sQuery(id+"F0.wireOp",EDGE,"E1.2.0.327"),sQuery(id+"F0.wireOp",EDGE,"E1.2.0.328"),sQuery(id+"F0.wireOp",EDGE,"E1.2.0.333"),sQuery(id+"F0.wireOp",EDGE,"E1.2.0.337"),sQuery(id+"F0.wireOp",EDGE,"E1.2.0.340"),sQuery(id+"F0.wireOp",EDGE,"E1.2.0.343"),sQuery(id+"F0.wireOp",EDGE,"E1.2.0.345"),sQuery(id+"F0.wireOp",EDGE,"E1.2.0.349"),sQuery(id+"F0.wireOp",EDGE,"E1.2.0.356"),sQuery(id+"F0.wireOp",EDGE,"E1.2.0.357"),sQuery(id+"F0.wireOp",EDGE,"E1.2.0.363"),sQuery(id+"F0.wireOp",EDGE,"E1.2.0.369"),sQuery(id+"F0.wireOp",EDGE,"E1.2.0.371"),sQuery(id+"F0.wireOp",EDGE,"E1.2.0.374"),sQuery(id+"F0.wireOp",EDGE,"E1.2.0.375"),sQuery(id+"F0.wireOp",EDGE,"E1.2.0.377"),sQuery(id+"F0.wireOp",EDGE,"E1.2.0.382"),sQuery(id+"F0.wireOp",EDGE,"E1.2.0.383"),sQuery(id+"F0.wireOp",EDGE,"E1.2.0.385"),sQuery(id+"F0.wireOp",EDGE,"E1.2.0.386"),sQuery(id+"F0.wireOp",EDGE,"E1.2.0.390"),sQuery(id+"F0.wireOp",EDGE,"E1.2.0.397"),sQuery(id+"F0.wireOp",EDGE,"E1.2.0.399"),sQuery(id+"F0.wireOp",EDGE,"E1.2.0.402"),sQuery(id+"F0.wireOp",EDGE,"E1.2.0.403"),sQuery(id+"F0.wireOp",EDGE,"E1.2.0.410"),sQuery(id+"F0.wireOp",EDGE,"E1.2.0.418"),sQuery(id+"F0.wireOp",EDGE,"E1.2.0.421"),sQuery(id+"F0.wireOp",EDGE,"E1.2.0.423"),sQuery(id+"F0.wireOp",EDGE,"E1.2.0.426"),sQuery(id+"F0.wireOp",EDGE,"E1.2.0.430"),sQuery(id+"F0.wireOp",EDGE,"E1.2.0.432"),sQuery(id+"F0.wireOp",EDGE,"E2.163.3.0"),sQuery(id+"F0.wireOp",EDGE,"E2.166.3.0"),sQuery(id+"F0.wireOp",EDGE,"E2.169.3.0"),sQuery(id+"F0.wireOp",EDGE,"E2.178.3.0"),sQuery(id+"F0.wireOp",EDGE,"E2.193.3.0"),sQuery(id+"F0.wireOp",EDGE,"E2.199.3.0"),sQuery(id+"F0.wireOp",EDGE,"E2.202.3.0"),sQuery(id+"F0.wireOp",EDGE,"E2.205.3.0"),sQuery(id+"F0.wireOp",EDGE,"E2.209.3.0"),sQuery(id+"F0.wireOp",EDGE,"E2.212.3.0"),sQuery(id+"F0.wireOp",EDGE,"E2.221.3.0"),sQuery(id+"F0.wireOp",EDGE,"E2.263.3.0"),sQuery(id+"F0.wireOp",EDGE,"E2.328.3.0"),sQuery(id+"F0.wireOp",EDGE,"E2.332.3.0"),sQuery(id+"F0.wireOp",EDGE,"E2.370.3.0"),sQuery(id+"F0.wireOp",EDGE,"E2.373.3.0"),sQuery(id+"F0.wireOp",EDGE,"E2.379.3.0"),sQuery(id+"F0.wireOp",EDGE,"E2.404.3.0"),sQuery(id+"F0.wireOp",EDGE,"E2.413.3.0"),sQuery(id+"F0.wireOp",EDGE,"E2.416.3.0"),sQuery(id+"F0.wireOp",EDGE,"E2.420.3.0"),sQuery(id+"F0.wireOp",EDGE,"E2.437.3.0"),sQuery(id+"F0.wireOp",EDGE,"E2.440.3.0"),sQuery(id+"F0.wireOp",EDGE,"E2.443.3.0"),sQuery(id+"F0.wireOp",EDGE,"E2.463.3.0"),sQuery(id+"F0.wireOp",EDGE,"E2.469.3.0"),sQuery(id+"F0.wireOp",EDGE,"E2.472.3.0"),sQuery(id+"F0.wireOp",EDGE,"E2.485.3.0"),sQuery(id+"F0.wireOp",EDGE,"E2.502.3.0"),sQuery(id+"F0.wireOp",EDGE,"E2.520.3.0"),sQuery(id+"F0.wireOp",EDGE,"E2.530.3.0"),sQuery(id+"F0.wireOp",EDGE,"E2.554.3.0"),sQuery(id+"F0.wireOp",EDGE,"E2.564.3.0"),sQuery(id+"F0.wireOp",EDGE,"E2.567.3.0"),sQuery(id+"F0.wireOp",EDGE,"E2.571.3.0"),sQuery(id+"F0.wireOp",EDGE,"E2.577.3.0"),sQuery(id+"F0.wireOp",EDGE,"E2.580.3.0"),sQuery(id+"F0.wireOp",EDGE,"E2.586.3.0"),sQuery(id+"F0.wireOp",EDGE,"E2.596.3.0"),sQuery(id+"F0.wireOp",EDGE,"E2.600.3.0"),sQuery(id+"F0.wireOp",EDGE,"E2.607.3.0"),sQuery(id+"F0.wireOp",EDGE,"E2.618.3.0"),sQuery(id+"F0.wireOp",EDGE,"E2.622.3.0"),sQuery(id+"F0.wireOp",EDGE,"E2.645.3.0"),sQuery(id+"F0.wireOp",EDGE,"E2.648.3.0"),sQuery(id+"F0.wireOp",EDGE,"E2.658.3.0"),sQuery(id+"F0.wireOp",EDGE,"E2.665.3.0"),sQuery(id+"F0.wireOp",EDGE,"E2.693.3.0"),sQuery(id+"F0.wireOp",EDGE,"E2.696.3.0"),sQuery(id+"F0.wireOp",EDGE,"E2.699.3.0"),sQuery(id+"F0.wireOp",EDGE,"E2.715.3.0"),sQuery(id+"F0.wireOp",EDGE,"E2.730.3.0"),sQuery(id+"F0.wireOp",EDGE,"E2.742.3.0"),sQuery(id+"F0.wireOp",EDGE,"E2.751.3.0"),sQuery(id+"F0.wireOp",EDGE,"E2.758.3.0"),sQuery(id+"F0.wireOp",EDGE,"E2.773.3.0"),sQuery(id+"F0.wireOp",EDGE,"E2.799.3.0"),sQuery(id+"F0.wireOp",EDGE,"E2.803.3.0"),sQuery(id+"F0.wireOp",EDGE,"E2.825.3.0"),sQuery(id+"F0.wireOp",EDGE,"E2.848.3.0"),sQuery(id+"F0.wireOp",EDGE,"E2.855.3.0"),sQuery(id+"F0.wireOp",EDGE,"E2.866.3.0"),sQuery(id+"F0.wireOp",EDGE,"E2.870.3.0"),sQuery(id+"F0.wireOp",EDGE,"E2.877.3.0"),sQuery(id+"F0.wireOp",EDGE,"E2.894.3.0"),sQuery(id+"F0.wireOp",EDGE,"E2.904.3.0"),sQuery(id+"F0.wireOp",EDGE,"E2.907.3.0"),sQuery(id+"F0.wireOp",EDGE,"E2.922.3.0"),sQuery(id+"F0.wireOp",EDGE,"E2.947.3.0"),sQuery(id+"F0.wireOp",EDGE,"E2.965.3.0"),sQuery(id+"F0.wireOp",EDGE,"E2.992.3.0"),sQuery(id+"F0.wireOp",EDGE,"E2.1020.3.0"),sQuery(id+"F0.wireOp",EDGE,"E2.1038.3.0"),sQuery(id+"F0.wireOp",EDGE,"E2.1049.3.0"),sQuery(id+"F0.wireOp",EDGE,"E2.1063.3.0"),sQuery(id+"F0.wireOp",EDGE,"E2.1070.3.0"),sQuery(id+"F0.wireOp",EDGE,"E3"),sQuery(id+"F0.wireOp",EDGE,"E4"),sQuery(id+"F0.wireOp",EDGE,"E5"),sQuery(id+"F0.wireOp",EDGE,"E6"),sQuery(id+"F0.wireOp",EDGE,"E7"),sQuery(id+"F0.wireOp",EDGE,"E8"),sQuery(id+"F0.wireOp",EDGE,"E9"),sQuery(id+"F0.wireOp",EDGE,"E10"),sQuery(id+"F0.wireOp",EDGE,"E11"),sQuery(id+"F0.wireOp",EDGE,"E12"),sQuery(id+"F0.wireOp",EDGE,"E13"),sQuery(id+"F0.wireOp",EDGE,"E14"),sQuery(id+"F0.wireOp",EDGE,"E15"),sQuery(id+"F0.wireOp",EDGE,"E16"),sQuery(id+"F0.wireOp",EDGE,"E17"),sQuery(id+"F0.wireOp",EDGE,"E18"),sQuery(id+"F0.wireOp",EDGE,"E19"),sQuery(id+"F0.wireOp",EDGE,"E20"),sQuery(id+"F0.wireOp",EDGE,"E21"),sQuery(id+"F0.wireOp",EDGE,"E22"),sQuery(id+"F0.wireOp",EDGE,"E23"),sQuery(id+"F0.wireOp",EDGE,"E24"),sQuery(id+"F0.wireOp",EDGE,"E25"),sQuery(id+"F0.wireOp",EDGE,"E26"),sQuery(id+"F0.wireOp",EDGE,"E27"),sQuery(id+"F0.wireOp",EDGE,"E28"),sQuery(id+"F0.wireOp",EDGE,"E29"),sQuery(id+"F0.wireOp",EDGE,"E30"),sQuery(id+"F0.wireOp",EDGE,"E31"),sQuery(id+"F0.wireOp",EDGE,"E32"),sQuery(id+"F0.wireOp",EDGE,"E33"),sQuery(id+"F0.wireOp",EDGE,"E34"),sQuery(id+"F0.wireOp",EDGE,"E35"),sQuery(id+"F0.wireOp",EDGE,"E36"),sQuery(id+"F0.wireOp",EDGE,"E37"),sQuery(id+"F0.wireOp",EDGE,"E38"),sQuery(id+"F0.wireOp",EDGE,"E39"),sQuery(id+"F0.wireOp",EDGE,"E40"),sQuery(id+"F0.wireOp",EDGE,"E41"),sQuery(id+"F0.wireOp",EDGE,"E42"),sQuery(id+"F0.wireOp",EDGE,"E43"),sQuery(id+"F0.wireOp",EDGE,"E44"),sQuery(id+"F0.wireOp",EDGE,"E45"),sQuery(id+"F0.wireOp",EDGE,"E46"),sQuery(id+"F0.wireOp",EDGE,"E47"),sQuery(id+"F0.wireOp",EDGE,"E48"),sQuery(id+"F0.wireOp",EDGE,"E49"),sQuery(id+"F0.wireOp",EDGE,"E50"),sQuery(id+"F0.wireOp",EDGE,"E51"),sQuery(id+"F0.wireOp",EDGE,"E52.filletArc"),sQuery(id+"F0.wireOp",EDGE,"E53.filletArc"),sQuery(id+"F0.wireOp",EDGE,"E54.filletArc"),sQuery(id+"F0.wireOp",EDGE,"E55.filletArc"),sQuery(id+"F0.wireOp",EDGE,"E56.filletArc"),sQuery(id+"F0.wireOp",EDGE,"E57.filletArc"),sQuery(id+"F0.wireOp",EDGE,"E58.filletArc"),sQuery(id+"F0.wireOp",EDGE,"E59.filletArc"),sQuery(id+"F0.wireOp",EDGE,"E60.trimOffspring"),sQuery(id+"F0.wireOp",EDGE,"E61.filletArc"),sQuery(id+"F0.wireOp",EDGE,"E62.filletArc")])],"isStart":false});
            var sketch = newSketch(context, id + "F4", { "sketchPlane" : qUnion([Q0])});
            skLineSegment(sketch, "E67.bottom", {"start": v(46.64, 31.64) * mm, "end": v(43.68, 31.64) * mm});
            skLineSegment(sketch, "E67.top", {"start": v(46.64, 27.4) * mm, "end": v(43.68, 27.4) * mm});
            skLineSegment(sketch, "E67.left", {"start": v(46.64, 31.64) * mm, "end": v(46.64, 27.4) * mm});
            skLineSegment(sketch, "E67.right", {"start": v(42.62, 30.59) * mm, "end": v(42.62, 28.45) * mm});
            skPoint(sketch, "E68.visualSharp", {"position": v(42.62, 31.64) * mm});
            skArc(sketch, "E68.filletArc", {"start": v(43.68, 31.64) * mm, "mid": v(42.93, 31.33) * mm, "end": v(42.62, 30.59) * mm});
            skPoint(sketch, "E69.visualSharp", {"position": v(42.62, 27.4) * mm});
            skArc(sketch, "E69.filletArc", {"start": v(42.62, 28.45) * mm, "mid": v(42.93, 27.7) * mm, "end": v(43.68, 27.4) * mm});
            skSolve(sketch);
        }
        {
            var Q0;
            {var subQ4=makeQuery(id+"F1.opExtrude","CAP_EDGE",EDGE,{"disambiguationData":[OSD([sQuery(id+"F0.wireOp",EDGE,"E51")])],"isStart":false});Q0=makeQuery(id+"F4.imprint","IMPRINT",FACE,{"disambiguationData":[TD([[makeQuery(id+"F4.imprint","IMPRINT",EDGE,{"derivedFrom":subQ4}),-1.0]])]});}
            extrude(context, id + "F5", {"entities" : qUnion([Q0]), "operationType" : NewBodyOperationType.ADD, "depth" : .5 * mm, "offsetDistance" : 25 * mm});
        }
        {
            var Q0;
            Q0=makeQuery(id+"F5.opExtrude","CAP_FACE",FACE,{"disambiguationData":[OSD([sQuery(id+"F0.wireOp",EDGE,"E51"),sQuery(id+"F0.wireOp",EDGE,"E52.filletArc"),sQuery(id+"F0.wireOp",EDGE,"E53.filletArc"),sQuery(id+"F4.wireOp",EDGE,"E67.bottom"),sQuery(id+"F4.wireOp",EDGE,"E67.top"),sQuery(id+"F4.wireOp",EDGE,"E67.left")])],"isStart":false});
            var sketch = newSketch(context, id + "F6", { "sketchPlane" : qUnion([Q0])});
            skLineSegment(sketch, "E70.bottom", {"start": v(46.36, 31.29) * mm, "end": v(44, 31.29) * mm});
            skLineSegment(sketch, "E70.top", {"start": v(46.36, 27.68) * mm, "end": v(44, 27.68) * mm});
            skLineSegment(sketch, "E70.left", {"start": v(46.36, 31.29) * mm, "end": v(46.36, 27.68) * mm});
            skLineSegment(sketch, "E70.right", {"start": v(43.03, 30.33) * mm, "end": v(43.03, 28.64) * mm});
            skPoint(sketch, "E71.visualSharp", {"position": v(43.03, 31.29) * mm});
            skArc(sketch, "E71.filletArc", {"start": v(44, 31.29) * mm, "mid": v(43.31, 31) * mm, "end": v(43.03, 30.33) * mm});
            skPoint(sketch, "E72.visualSharp", {"position": v(43.03, 27.68) * mm});
            skArc(sketch, "E72.filletArc", {"start": v(43.03, 28.64) * mm, "mid": v(43.31, 27.96) * mm, "end": v(44, 27.68) * mm});
            skSolve(sketch);
        }
        {
            var Q0;
            Q0 = qSketchRegion(id + "F6", true);
            extrude(context, id + "F7", {"entities" : qUnion([Q0]), "operationType" : NewBodyOperationType.REMOVE, "depth" : -.5 * mm, "offsetDistance" : 25 * mm});
        }
    });
